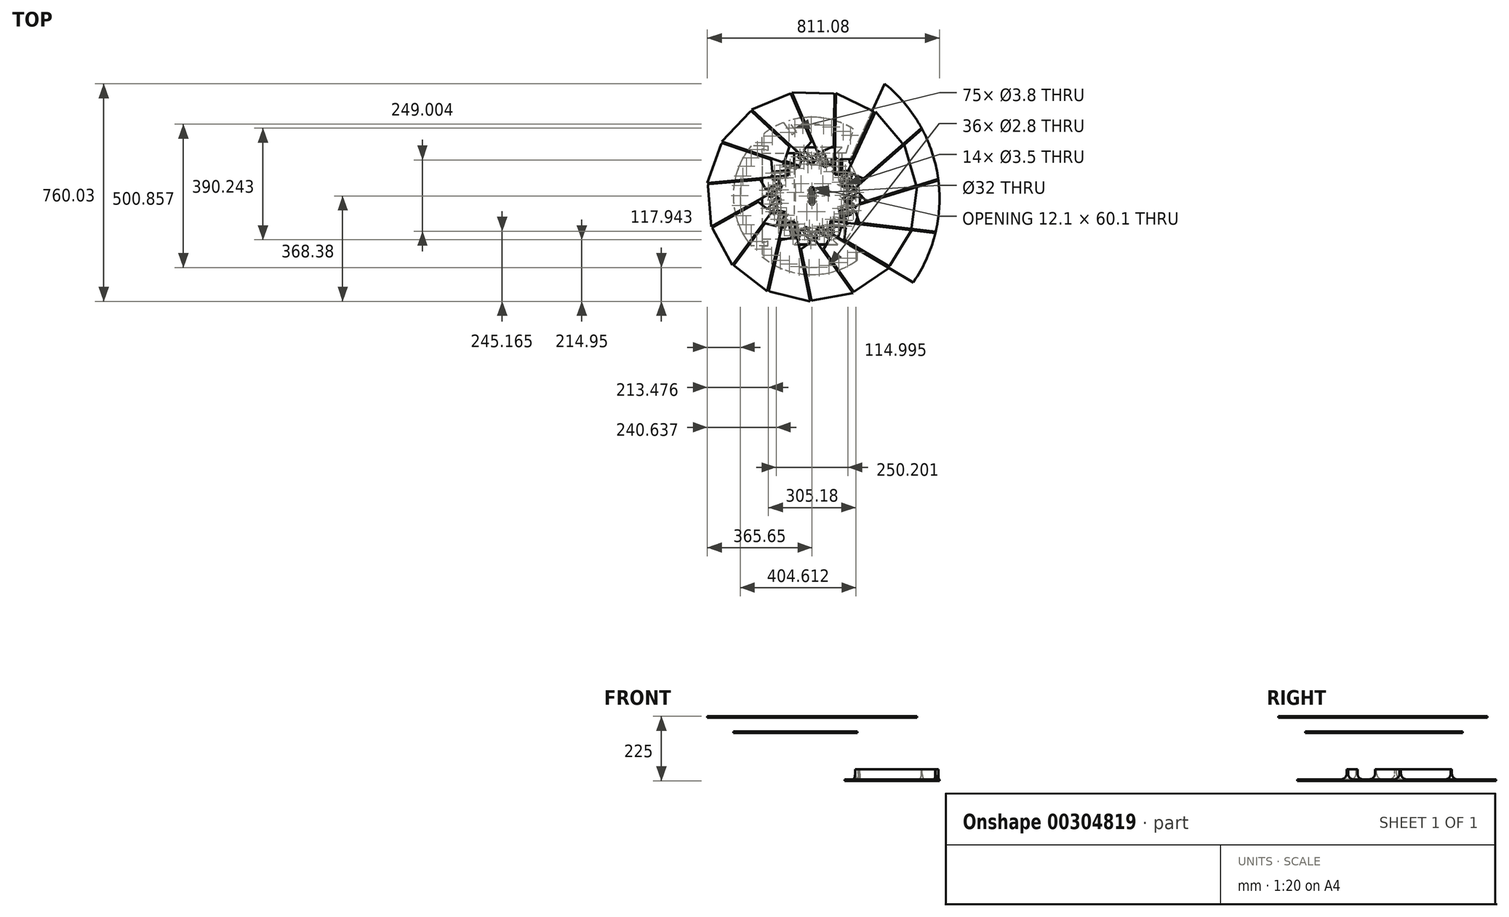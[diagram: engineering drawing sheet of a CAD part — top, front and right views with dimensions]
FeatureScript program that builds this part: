
annotation { "Feature Type Name" : "Feature", "Feature Type Description" : "" }
export const myFeature = defineFeature(function(context is Context, id is Id, definition is map)
    precondition{}
    {
        {
            var Q0;
            Q0=qCreatedBy(makeId("Top.planeOp"),FACE);
            var sketch = newSketch(context, id + "F0", { "sketchPlane" : qUnion([Q0])});
            skLineSegment(sketch, "E0", {"start": v(-97.83, 116.22) * mm, "end": v(-45.75, 98.54) * mm});
            skLineSegment(sketch, "E1", {"start": v(-78.6, 172.89) * mm, "end": v(-209.62, 294) * mm});
            skPoint(sketch, "E2.visualSharp", {"position": v(-213.23, 297.34) * mm});
            skArc(sketch, "E2.filletArc", {"start": v(-209.62, 294) * mm, "mid": v(-213.17, 295.33) * mm, "end": v(-216.63, 293.79) * mm});
            skLineSegment(sketch, "E3", {"start": v(-101.62, 117.5) * mm, "end": v(-315.6, 190.14) * mm});
            skLineSegment(sketch, "E4", {"start": v(-315.6, 190.14) * mm, "end": v(-216.63, 293.79) * mm});
            skLineSegment(sketch, "E5", {"start": v(-43.7, 117.06) * mm, "end": v(-91.98, 133.45) * mm});
            skLineSegment(sketch, "E6", {"start": v(-91.98, 133.45) * mm, "end": v(-78.6, 172.89) * mm});
            skLineSegment(sketch, "E7.bottom", {"start": v(4.05, -30.05) * mm, "end": v(-4.05, -30.05) * mm});
            skLineSegment(sketch, "E7.top", {"start": v(4.05, 30.05) * mm, "end": v(-4.05, 30.05) * mm});
            skLineSegment(sketch, "E7.left", {"start": v(6.05, -28.05) * mm, "end": v(6.05, 28.05) * mm});
            skLineSegment(sketch, "E7.right", {"start": v(-6.05, -28.05) * mm, "end": v(-6.05, 28.05) * mm});
            skPoint(sketch, "E7.middle", {"position": v(0, 0) * mm});
            skPoint(sketch, "E8.visualSharp", {"position": v(-6.05, 30.05) * mm});
            skArc(sketch, "E8.filletArc", {"start": v(-4.05, 30.05) * mm, "mid": v(-5.46, 29.46) * mm, "end": v(-6.05, 28.05) * mm});
            skPoint(sketch, "E9.visualSharp", {"position": v(6.05, 30.05) * mm});
            skArc(sketch, "E9.filletArc", {"start": v(6.05, 28.05) * mm, "mid": v(5.46, 29.46) * mm, "end": v(4.05, 30.05) * mm});
            skPoint(sketch, "E10.visualSharp", {"position": v(-6.05, -30.05) * mm});
            skArc(sketch, "E10.filletArc", {"start": v(-6.05, -28.05) * mm, "mid": v(-5.46, -29.46) * mm, "end": v(-4.05, -30.05) * mm});
            skPoint(sketch, "E11.visualSharp", {"position": v(6.05, -30.05) * mm});
            skArc(sketch, "E11.filletArc", {"start": v(4.05, -30.05) * mm, "mid": v(5.46, -29.46) * mm, "end": v(6.05, -28.05) * mm});
            skLineSegment(sketch, "E12.bottom", {"start": v(-101.63, 105.04) * mm, "end": v(-91.98, 133.45) * mm});
            skLineSegment(sketch, "E12.top", {"start": v(-53.33, 88.65) * mm, "end": v(-43.7, 117.06) * mm});
            skLineSegment(sketch, "E12.left", {"start": v(-101.63, 105.04) * mm, "end": v(-53.33, 88.65) * mm});
            skLineSegment(sketch, "E12.right", {"start": v(-91.98, 133.45) * mm, "end": v(-43.7, 117.06) * mm});
            skCircle(sketch, "E13", {"center": v(-51.93, 114.57) * mm, "radius": 1.75 * mm});
            skCircle(sketch, "E14", {"center": v(-86.96, 126.47) * mm, "radius": 1.9 * mm});
            skCircle(sketch, "E15", {"center": v(-93.4, 107.53) * mm, "radius": 1.9 * mm});
            skCircle(sketch, "E16", {"center": v(-58.36, 95.64) * mm, "radius": 1.9 * mm});
            skPoint(sketch, "E17", {"position": v(-77.48, 96.85) * mm});
            skLineSegment(sketch, "E18.left", {"start": v(-97.51, 117.17) * mm, "end": v(-49.22, 100.77) * mm});
            skLineSegment(sketch, "E18.right", {"start": v(-96.1, 121.33) * mm, "end": v(-47.8, 104.94) * mm});
            skLineSegment(sketch, "E19.0", {"start": v(-58.36, 95.64) * mm, "end": v(-51.93, 114.57) * mm, "construction": true});
            skLineSegment(sketch, "E20.0", {"start": v(-93.4, 107.53) * mm, "end": v(-86.96, 126.47) * mm, "construction": true});
            skLineSegment(sketch, "E21.0", {"start": v(-58.36, 95.64) * mm, "end": v(-93.4, 107.53) * mm, "construction": true});
            skLineSegment(sketch, "E22.0", {"start": v(-51.93, 114.57) * mm, "end": v(-86.96, 126.47) * mm, "construction": true});
            skPoint(sketch, "E23", {"position": v(-96.8, 119.25) * mm});
            skCircle(sketch, "E24", {"center": v(-75.87, 101.58) * mm, "radius": 1.9 * mm});
            skCircle(sketch, "E25", {"center": v(-69.45, 120.52) * mm, "radius": 1.9 * mm});
            skCircle(sketch, "E26.1.0", {"center": v(-130.88, 80.16) * mm, "radius": 1.9 * mm});
            skLineSegment(sketch, "E26.1.1", {"start": v(-92.2, 63.63) * mm, "end": v(-94.04, 83.55) * mm, "construction": true});
            skCircle(sketch, "E26.1.2", {"center": v(-112.46, 81.86) * mm, "radius": 1.9 * mm});
            skLineSegment(sketch, "E26.1.3", {"start": v(-92.2, 63.63) * mm, "end": v(-129.05, 60.25) * mm, "construction": true});
            skCircle(sketch, "E26.1.4", {"center": v(-110.63, 61.94) * mm, "radius": 1.9 * mm});
            skCircle(sketch, "E26.1.5", {"center": v(-92.2, 63.63) * mm, "radius": 1.9 * mm});
            skLineSegment(sketch, "E26.1.6", {"start": v(-135.57, 54.63) * mm, "end": v(-84.78, 59.3) * mm});
            skLineSegment(sketch, "E26.1.7", {"start": v(-135.57, 54.63) * mm, "end": v(-138.31, 84.5) * mm});
            skPoint(sketch, "E26.1.8", {"position": v(-136.94, 69.56) * mm});
            skLineSegment(sketch, "E26.1.9", {"start": v(-94.04, 83.55) * mm, "end": v(-130.88, 80.16) * mm, "construction": true});
            skLineSegment(sketch, "E26.1.10", {"start": v(-84.78, 59.3) * mm, "end": v(-87.53, 89.17) * mm});
            skCircle(sketch, "E26.1.11", {"center": v(-129.05, 60.25) * mm, "radius": 1.9 * mm});
            skLineSegment(sketch, "E26.1.12", {"start": v(-129.05, 60.25) * mm, "end": v(-130.88, 80.16) * mm, "construction": true});
            skPoint(sketch, "E26.1.13", {"position": v(-110.17, 56.96) * mm});
            skCircle(sketch, "E26.1.14", {"center": v(-94.04, 83.55) * mm, "radius": 1.75 * mm});
            skLineSegment(sketch, "E26.1.15", {"start": v(-138.31, 84.5) * mm, "end": v(-87.53, 89.17) * mm});
            skLineSegment(sketch, "E26.1.16", {"start": v(-136.74, 67.37) * mm, "end": v(-85.95, 72.04) * mm});
            skLineSegment(sketch, "E26.1.17", {"start": v(-137.14, 71.75) * mm, "end": v(-86.35, 76.42) * mm});
            skCircle(sketch, "E26.2.0", {"center": v(-152.17, 20) * mm, "radius": 1.9 * mm});
            skLineSegment(sketch, "E26.2.1", {"start": v(-110.12, 20.63) * mm, "end": v(-119.9, 38.08) * mm, "construction": true});
            skCircle(sketch, "E26.2.2", {"center": v(-136.03, 29.04) * mm, "radius": 1.9 * mm});
            skLineSegment(sketch, "E26.2.3", {"start": v(-110.12, 20.63) * mm, "end": v(-142.4, 2.55) * mm, "construction": true});
            skCircle(sketch, "E26.2.4", {"center": v(-126.26, 11.59) * mm, "radius": 1.9 * mm});
            skCircle(sketch, "E26.2.5", {"center": v(-110.12, 20.63) * mm, "radius": 1.9 * mm});
            skLineSegment(sketch, "E26.2.6", {"start": v(-146.07, -5.24) * mm, "end": v(-101.57, 19.68) * mm});
            skLineSegment(sketch, "E26.2.7", {"start": v(-146.07, -5.24) * mm, "end": v(-160.72, 20.94) * mm});
            skPoint(sketch, "E26.2.8", {"position": v(-153.4, 7.85) * mm});
            skLineSegment(sketch, "E26.2.9", {"start": v(-119.9, 38.08) * mm, "end": v(-152.17, 20) * mm, "construction": true});
            skLineSegment(sketch, "E26.2.10", {"start": v(-101.57, 19.68) * mm, "end": v(-116.23, 45.86) * mm});
            skCircle(sketch, "E26.2.11", {"center": v(-142.4, 2.55) * mm, "radius": 1.9 * mm});
            skLineSegment(sketch, "E26.2.12", {"start": v(-142.4, 2.55) * mm, "end": v(-152.17, 20) * mm, "construction": true});
            skPoint(sketch, "E26.2.13", {"position": v(-123.82, 7.22) * mm});
            skCircle(sketch, "E26.2.14", {"center": v(-119.9, 38.08) * mm, "radius": 1.75 * mm});
            skLineSegment(sketch, "E26.2.15", {"start": v(-160.72, 20.94) * mm, "end": v(-116.23, 45.86) * mm});
            skLineSegment(sketch, "E26.2.16", {"start": v(-152.32, 5.93) * mm, "end": v(-107.82, 30.85) * mm});
            skLineSegment(sketch, "E26.2.17", {"start": v(-154.47, 9.77) * mm, "end": v(-109.97, 34.7) * mm});
            skCircle(sketch, "E26.3.0", {"center": v(-147.15, -43.63) * mm, "radius": 1.9 * mm});
            skLineSegment(sketch, "E26.3.1", {"start": v(-108.99, -25.95) * mm, "end": v(-125.01, -13.98) * mm, "construction": true});
            skCircle(sketch, "E26.3.2", {"center": v(-136.08, -28.8) * mm, "radius": 1.9 * mm});
            skLineSegment(sketch, "E26.3.3", {"start": v(-108.99, -25.95) * mm, "end": v(-131.13, -55.6) * mm, "construction": true});
            skCircle(sketch, "E26.3.4", {"center": v(-120.06, -40.77) * mm, "radius": 1.9 * mm});
            skCircle(sketch, "E26.3.5", {"center": v(-108.99, -25.95) * mm, "radius": 1.9 * mm});
            skLineSegment(sketch, "E26.3.6", {"start": v(-131.3, -64.2) * mm, "end": v(-100.8, -23.33) * mm});
            skLineSegment(sketch, "E26.3.7", {"start": v(-131.3, -64.2) * mm, "end": v(-155.35, -46.24) * mm});
            skPoint(sketch, "E26.3.8", {"position": v(-143.33, -55.22) * mm});
            skLineSegment(sketch, "E26.3.9", {"start": v(-125.01, -13.98) * mm, "end": v(-147.15, -43.63) * mm, "construction": true});
            skLineSegment(sketch, "E26.3.10", {"start": v(-100.8, -23.33) * mm, "end": v(-124.83, -5.38) * mm});
            skCircle(sketch, "E26.3.11", {"center": v(-131.13, -55.6) * mm, "radius": 1.9 * mm});
            skLineSegment(sketch, "E26.3.12", {"start": v(-131.13, -55.6) * mm, "end": v(-147.15, -43.63) * mm, "construction": true});
            skPoint(sketch, "E26.3.13", {"position": v(-116.05, -43.76) * mm});
            skCircle(sketch, "E26.3.14", {"center": v(-125.01, -13.98) * mm, "radius": 1.75 * mm});
            skLineSegment(sketch, "E26.3.15", {"start": v(-155.35, -46.24) * mm, "end": v(-124.83, -5.38) * mm});
            skLineSegment(sketch, "E26.3.16", {"start": v(-141.56, -56.53) * mm, "end": v(-111.05, -15.67) * mm});
            skLineSegment(sketch, "E26.3.17", {"start": v(-145.09, -53.9) * mm, "end": v(-114.57, -13.04) * mm});
            skCircle(sketch, "E26.4.0", {"center": v(-116.68, -99.7) * mm, "radius": 1.9 * mm});
            skLineSegment(sketch, "E26.4.1", {"start": v(-89.01, -68.03) * mm, "end": v(-108.52, -63.62) * mm, "construction": true});
            skCircle(sketch, "E26.4.2", {"center": v(-112.6, -81.66) * mm, "radius": 1.9 * mm});
            skLineSegment(sketch, "E26.4.3", {"start": v(-89.01, -68.03) * mm, "end": v(-97.18, -104.12) * mm, "construction": true});
            skCircle(sketch, "E26.4.4", {"center": v(-93.1, -86.08) * mm, "radius": 1.9 * mm});
            skCircle(sketch, "E26.4.5", {"center": v(-89.01, -68.03) * mm, "radius": 1.9 * mm});
            skLineSegment(sketch, "E26.4.6", {"start": v(-93.85, -112.05) * mm, "end": v(-82.6, -62.3) * mm});
            skLineSegment(sketch, "E26.4.7", {"start": v(-93.85, -112.05) * mm, "end": v(-123.1, -105.43) * mm});
            skPoint(sketch, "E26.4.8", {"position": v(-108.48, -108.74) * mm});
            skLineSegment(sketch, "E26.4.9", {"start": v(-108.52, -63.62) * mm, "end": v(-116.68, -99.7) * mm, "construction": true});
            skLineSegment(sketch, "E26.4.10", {"start": v(-82.6, -62.3) * mm, "end": v(-111.85, -55.69) * mm});
            skCircle(sketch, "E26.4.11", {"center": v(-97.18, -104.12) * mm, "radius": 1.9 * mm});
            skLineSegment(sketch, "E26.4.12", {"start": v(-97.18, -104.12) * mm, "end": v(-116.68, -99.7) * mm, "construction": true});
            skPoint(sketch, "E26.4.13", {"position": v(-88.22, -87.18) * mm});
            skCircle(sketch, "E26.4.14", {"center": v(-108.52, -63.62) * mm, "radius": 1.75 * mm});
            skLineSegment(sketch, "E26.4.15", {"start": v(-123.1, -105.43) * mm, "end": v(-111.85, -55.69) * mm});
            skLineSegment(sketch, "E26.4.16", {"start": v(-106.33, -109.23) * mm, "end": v(-95.07, -59.48) * mm});
            skLineSegment(sketch, "E26.4.17", {"start": v(-110.62, -108.26) * mm, "end": v(-99.37, -58.51) * mm});
            skCircle(sketch, "E26.5.0", {"center": v(-66.04, -138.55) * mm, "radius": 1.9 * mm});
            skLineSegment(sketch, "E26.5.1", {"start": v(-53.65, -98.36) * mm, "end": v(-73.26, -102.26) * mm, "construction": true});
            skCircle(sketch, "E26.5.2", {"center": v(-69.65, -120.4) * mm, "radius": 1.9 * mm});
            skLineSegment(sketch, "E26.5.3", {"start": v(-53.65, -98.36) * mm, "end": v(-46.43, -134.64) * mm, "construction": true});
            skCircle(sketch, "E26.5.4", {"center": v(-50.04, -116.5) * mm, "radius": 1.9 * mm});
            skCircle(sketch, "E26.5.5", {"center": v(-53.65, -98.36) * mm, "radius": 1.9 * mm});
            skLineSegment(sketch, "E26.5.6", {"start": v(-40.16, -140.53) * mm, "end": v(-50.1, -90.51) * mm});
            skLineSegment(sketch, "E26.5.7", {"start": v(-40.16, -140.53) * mm, "end": v(-69.58, -146.39) * mm});
            skPoint(sketch, "E26.5.8", {"position": v(-54.87, -143.46) * mm});
            skLineSegment(sketch, "E26.5.9", {"start": v(-73.26, -102.26) * mm, "end": v(-66.04, -138.55) * mm, "construction": true});
            skLineSegment(sketch, "E26.5.10", {"start": v(-50.1, -90.51) * mm, "end": v(-79.53, -96.37) * mm});
            skCircle(sketch, "E26.5.11", {"center": v(-46.43, -134.64) * mm, "radius": 1.9 * mm});
            skLineSegment(sketch, "E26.5.12", {"start": v(-46.43, -134.64) * mm, "end": v(-66.04, -138.55) * mm, "construction": true});
            skPoint(sketch, "E26.5.13", {"position": v(-45.13, -115.52) * mm});
            skCircle(sketch, "E26.5.14", {"center": v(-73.26, -102.26) * mm, "radius": 1.75 * mm});
            skLineSegment(sketch, "E26.5.15", {"start": v(-69.58, -146.39) * mm, "end": v(-79.53, -96.37) * mm});
            skLineSegment(sketch, "E26.5.16", {"start": v(-52.71, -143.03) * mm, "end": v(-62.66, -93.01) * mm});
            skLineSegment(sketch, "E26.5.17", {"start": v(-57.03, -143.9) * mm, "end": v(-66.98, -93.87) * mm});
            skCircle(sketch, "E26.6.0", {"center": v(-3.98, -153.43) * mm, "radius": 1.9 * mm});
            skLineSegment(sketch, "E26.6.1", {"start": v(-9, -111.67) * mm, "end": v(-25.34, -123.21) * mm, "construction": true});
            skCircle(sketch, "E26.6.2", {"center": v(-14.66, -138.32) * mm, "radius": 1.9 * mm});
            skLineSegment(sketch, "E26.6.3", {"start": v(-9, -111.67) * mm, "end": v(12.35, -141.89) * mm, "construction": true});
            skCircle(sketch, "E26.6.4", {"center": v(1.67, -126.78) * mm, "radius": 1.9 * mm});
            skCircle(sketch, "E26.6.5", {"center": v(-9, -111.67) * mm, "radius": 1.9 * mm});
            skLineSegment(sketch, "E26.6.6", {"start": v(20.48, -144.72) * mm, "end": v(-8.96, -103.07) * mm});
            skLineSegment(sketch, "E26.6.7", {"start": v(20.48, -144.72) * mm, "end": v(-4.02, -162.03) * mm});
            skPoint(sketch, "E26.6.8", {"position": v(8.23, -153.38) * mm});
            skLineSegment(sketch, "E26.6.9", {"start": v(-25.34, -123.21) * mm, "end": v(-3.98, -153.43) * mm, "construction": true});
            skLineSegment(sketch, "E26.6.10", {"start": v(-8.96, -103.07) * mm, "end": v(-33.46, -120.38) * mm});
            skCircle(sketch, "E26.6.11", {"center": v(12.35, -141.89) * mm, "radius": 1.9 * mm});
            skLineSegment(sketch, "E26.6.12", {"start": v(12.35, -141.89) * mm, "end": v(-3.98, -153.43) * mm, "construction": true});
            skPoint(sketch, "E26.6.13", {"position": v(5.76, -123.9) * mm});
            skCircle(sketch, "E26.6.14", {"center": v(-25.34, -123.21) * mm, "radius": 1.75 * mm});
            skLineSegment(sketch, "E26.6.15", {"start": v(-4.02, -162.03) * mm, "end": v(-33.46, -120.38) * mm});
            skLineSegment(sketch, "E26.6.16", {"start": v(10.02, -152.1) * mm, "end": v(-19.41, -110.46) * mm});
            skLineSegment(sketch, "E26.6.17", {"start": v(6.43, -154.65) * mm, "end": v(-23, -113) * mm});
            skCircle(sketch, "E26.7.0", {"center": v(58.77, -141.78) * mm, "radius": 1.9 * mm});
            skLineSegment(sketch, "E26.7.1", {"start": v(37.2, -105.68) * mm, "end": v(26.97, -122.87) * mm, "construction": true});
            skCircle(sketch, "E26.7.2", {"center": v(42.87, -132.33) * mm, "radius": 1.9 * mm});
            skLineSegment(sketch, "E26.7.3", {"start": v(37.2, -105.68) * mm, "end": v(69, -124.6) * mm, "construction": true});
            skCircle(sketch, "E26.7.4", {"center": v(53.1, -115.14) * mm, "radius": 1.9 * mm});
            skCircle(sketch, "E26.7.5", {"center": v(37.2, -105.68) * mm, "radius": 1.9 * mm});
            skLineSegment(sketch, "E26.7.6", {"start": v(77.57, -123.88) * mm, "end": v(33.74, -97.8) * mm});
            skLineSegment(sketch, "E26.7.7", {"start": v(77.57, -123.88) * mm, "end": v(62.23, -149.66) * mm});
            skPoint(sketch, "E26.7.8", {"position": v(69.9, -136.77) * mm});
            skLineSegment(sketch, "E26.7.9", {"start": v(26.97, -122.87) * mm, "end": v(58.77, -141.78) * mm, "construction": true});
            skLineSegment(sketch, "E26.7.10", {"start": v(33.74, -97.8) * mm, "end": v(18.4, -123.58) * mm});
            skCircle(sketch, "E26.7.11", {"center": v(69, -124.6) * mm, "radius": 1.9 * mm});
            skLineSegment(sketch, "E26.7.12", {"start": v(69, -124.6) * mm, "end": v(58.77, -141.78) * mm, "construction": true});
            skPoint(sketch, "E26.7.13", {"position": v(55.65, -110.84) * mm});
            skCircle(sketch, "E26.7.14", {"center": v(26.97, -122.87) * mm, "radius": 1.75 * mm});
            skLineSegment(sketch, "E26.7.15", {"start": v(62.23, -149.66) * mm, "end": v(18.4, -123.58) * mm});
            skLineSegment(sketch, "E26.7.16", {"start": v(71.02, -134.88) * mm, "end": v(27.2, -108.8) * mm});
            skLineSegment(sketch, "E26.7.17", {"start": v(68.77, -138.66) * mm, "end": v(24.94, -112.58) * mm});
            skCircle(sketch, "E26.8.0", {"center": v(111.36, -105.62) * mm, "radius": 1.9 * mm});
            skLineSegment(sketch, "E26.8.1", {"start": v(76.96, -81.41) * mm, "end": v(74.61, -101.27) * mm, "construction": true});
            skCircle(sketch, "E26.8.2", {"center": v(92.99, -103.45) * mm, "radius": 1.9 * mm});
            skLineSegment(sketch, "E26.8.3", {"start": v(76.96, -81.41) * mm, "end": v(113.7, -85.76) * mm, "construction": true});
            skCircle(sketch, "E26.8.4", {"center": v(95.34, -83.59) * mm, "radius": 1.9 * mm});
            skCircle(sketch, "E26.8.5", {"center": v(76.96, -81.41) * mm, "radius": 1.9 * mm});
            skLineSegment(sketch, "E26.8.6", {"start": v(121.25, -81.62) * mm, "end": v(70.6, -75.62) * mm});
            skLineSegment(sketch, "E26.8.7", {"start": v(121.25, -81.62) * mm, "end": v(117.72, -111.41) * mm});
            skPoint(sketch, "E26.8.8", {"position": v(119.48, -96.52) * mm});
            skLineSegment(sketch, "E26.8.9", {"start": v(74.61, -101.27) * mm, "end": v(111.36, -105.62) * mm, "construction": true});
            skLineSegment(sketch, "E26.8.10", {"start": v(70.6, -75.62) * mm, "end": v(67.07, -105.42) * mm});
            skCircle(sketch, "E26.8.11", {"center": v(113.7, -85.76) * mm, "radius": 1.9 * mm});
            skLineSegment(sketch, "E26.8.12", {"start": v(113.7, -85.76) * mm, "end": v(111.36, -105.62) * mm, "construction": true});
            skPoint(sketch, "E26.8.13", {"position": v(95.92, -78.62) * mm});
            skCircle(sketch, "E26.8.14", {"center": v(74.61, -101.27) * mm, "radius": 1.75 * mm});
            skLineSegment(sketch, "E26.8.15", {"start": v(117.72, -111.41) * mm, "end": v(67.07, -105.42) * mm});
            skLineSegment(sketch, "E26.8.16", {"start": v(119.74, -94.33) * mm, "end": v(69.1, -88.34) * mm});
            skLineSegment(sketch, "E26.8.17", {"start": v(119.23, -98.7) * mm, "end": v(68.58, -92.7) * mm});
            skCircle(sketch, "E26.9.0", {"center": v(144.7, -51.2) * mm, "radius": 1.9 * mm});
            skLineSegment(sketch, "E26.9.1", {"start": v(103.42, -43.07) * mm, "end": v(109.35, -62.17) * mm, "construction": true});
            skCircle(sketch, "E26.9.2", {"center": v(127.02, -56.68) * mm, "radius": 1.9 * mm});
            skLineSegment(sketch, "E26.9.3", {"start": v(103.42, -43.07) * mm, "end": v(138.76, -32.1) * mm, "construction": true});
            skCircle(sketch, "E26.9.4", {"center": v(121.1, -37.58) * mm, "radius": 1.9 * mm});
            skCircle(sketch, "E26.9.5", {"center": v(103.42, -43.07) * mm, "radius": 1.9 * mm});
            skLineSegment(sketch, "E26.9.6", {"start": v(143.96, -25.25) * mm, "end": v(95.26, -40.37) * mm});
            skLineSegment(sketch, "E26.9.7", {"start": v(143.96, -25.25) * mm, "end": v(152.86, -53.9) * mm});
            skPoint(sketch, "E26.9.8", {"position": v(148.41, -39.57) * mm});
            skLineSegment(sketch, "E26.9.9", {"start": v(109.35, -62.17) * mm, "end": v(144.7, -51.2) * mm, "construction": true});
            skLineSegment(sketch, "E26.9.10", {"start": v(95.26, -40.37) * mm, "end": v(104.15, -69.02) * mm});
            skCircle(sketch, "E26.9.11", {"center": v(138.76, -32.1) * mm, "radius": 1.9 * mm});
            skLineSegment(sketch, "E26.9.12", {"start": v(138.76, -32.1) * mm, "end": v(144.7, -51.2) * mm, "construction": true});
            skPoint(sketch, "E26.9.13", {"position": v(119.6, -32.8) * mm});
            skCircle(sketch, "E26.9.14", {"center": v(109.35, -62.17) * mm, "radius": 1.75 * mm});
            skLineSegment(sketch, "E26.9.15", {"start": v(152.86, -53.9) * mm, "end": v(104.15, -69.02) * mm});
            skLineSegment(sketch, "E26.9.16", {"start": v(147.76, -37.47) * mm, "end": v(99.05, -52.6) * mm});
            skLineSegment(sketch, "E26.9.17", {"start": v(149.06, -41.67) * mm, "end": v(100.36, -56.8) * mm});
            skCircle(sketch, "E26.10.0", {"center": v(153, 12.08) * mm, "radius": 1.9 * mm});
            skLineSegment(sketch, "E26.10.1", {"start": v(112, 2.72) * mm, "end": v(125.19, -12.32) * mm, "construction": true});
            skCircle(sketch, "E26.10.2", {"center": v(139.1, -0.12) * mm, "radius": 1.9 * mm});
            skLineSegment(sketch, "E26.10.3", {"start": v(112, 2.72) * mm, "end": v(139.82, 27.12) * mm, "construction": true});
            skCircle(sketch, "E26.10.4", {"center": v(125.9, 14.92) * mm, "radius": 1.9 * mm});
            skCircle(sketch, "E26.10.5", {"center": v(112, 2.72) * mm, "radius": 1.9 * mm});
            skLineSegment(sketch, "E26.10.6", {"start": v(141.79, 35.5) * mm, "end": v(103.44, 1.86) * mm});
            skLineSegment(sketch, "E26.10.7", {"start": v(141.79, 35.5) * mm, "end": v(161.57, 12.93) * mm});
            skPoint(sketch, "E26.10.8", {"position": v(151.68, 24.21) * mm});
            skLineSegment(sketch, "E26.10.9", {"start": v(125.19, -12.32) * mm, "end": v(153, 12.08) * mm, "construction": true});
            skLineSegment(sketch, "E26.10.10", {"start": v(103.44, 1.86) * mm, "end": v(123.22, -20.7) * mm});
            skCircle(sketch, "E26.10.11", {"center": v(139.82, 27.12) * mm, "radius": 1.9 * mm});
            skLineSegment(sketch, "E26.10.12", {"start": v(139.82, 27.12) * mm, "end": v(153, 12.08) * mm, "construction": true});
            skPoint(sketch, "E26.10.13", {"position": v(122.61, 18.68) * mm});
            skCircle(sketch, "E26.10.14", {"center": v(125.19, -12.32) * mm, "radius": 1.75 * mm});
            skLineSegment(sketch, "E26.10.15", {"start": v(161.57, 12.93) * mm, "end": v(123.22, -20.7) * mm});
            skLineSegment(sketch, "E26.10.16", {"start": v(150.22, 25.87) * mm, "end": v(111.88, -7.76) * mm});
            skLineSegment(sketch, "E26.10.17", {"start": v(153.13, 22.56) * mm, "end": v(114.78, -11.07) * mm});
            skCircle(sketch, "E26.11.0", {"center": v(134.86, 73.27) * mm, "radius": 1.9 * mm});
            skLineSegment(sketch, "E26.11.1", {"start": v(101.21, 48.04) * mm, "end": v(119.37, 39.67) * mm, "construction": true});
            skCircle(sketch, "E26.11.2", {"center": v(127.12, 56.47) * mm, "radius": 1.9 * mm});
            skLineSegment(sketch, "E26.11.3", {"start": v(101.21, 48.04) * mm, "end": v(116.7, 81.64) * mm, "construction": true});
            skCircle(sketch, "E26.11.4", {"center": v(108.96, 64.84) * mm, "radius": 1.9 * mm});
            skCircle(sketch, "E26.11.5", {"center": v(101.21, 48.04) * mm, "radius": 1.9 * mm});
            skLineSegment(sketch, "E26.11.6", {"start": v(115.1, 90.1) * mm, "end": v(93.74, 43.78) * mm});
            skLineSegment(sketch, "E26.11.7", {"start": v(115.1, 90.1) * mm, "end": v(142.34, 77.53) * mm});
            skPoint(sketch, "E26.11.8", {"position": v(128.71, 83.81) * mm});
            skLineSegment(sketch, "E26.11.9", {"start": v(119.37, 39.67) * mm, "end": v(134.86, 73.27) * mm, "construction": true});
            skLineSegment(sketch, "E26.11.10", {"start": v(93.74, 43.78) * mm, "end": v(120.98, 31.22) * mm});
            skCircle(sketch, "E26.11.11", {"center": v(116.7, 81.64) * mm, "radius": 1.9 * mm});
            skLineSegment(sketch, "E26.11.12", {"start": v(116.7, 81.64) * mm, "end": v(134.86, 73.27) * mm, "construction": true});
            skPoint(sketch, "E26.11.13", {"position": v(104.42, 66.93) * mm});
            skCircle(sketch, "E26.11.14", {"center": v(119.37, 39.67) * mm, "radius": 1.75 * mm});
            skLineSegment(sketch, "E26.11.15", {"start": v(142.34, 77.53) * mm, "end": v(120.98, 31.22) * mm});
            skLineSegment(sketch, "E26.11.16", {"start": v(126.72, 84.73) * mm, "end": v(105.36, 38.42) * mm});
            skLineSegment(sketch, "E26.11.17", {"start": v(130.71, 82.9) * mm, "end": v(109.36, 36.57) * mm});
            skCircle(sketch, "E26.12.0", {"center": v(93.4, 121.79) * mm, "radius": 1.9 * mm});
            skLineSegment(sketch, "E26.12.1", {"start": v(72.92, 85.05) * mm, "end": v(92.92, 84.8) * mm, "construction": true});
            skCircle(sketch, "E26.12.2", {"center": v(93.16, 103.29) * mm, "radius": 1.9 * mm});
            skLineSegment(sketch, "E26.12.3", {"start": v(72.92, 85.05) * mm, "end": v(73.4, 122.05) * mm, "construction": true});
            skCircle(sketch, "E26.12.4", {"center": v(73.16, 103.55) * mm, "radius": 1.9 * mm});
            skCircle(sketch, "E26.12.5", {"center": v(72.92, 85.05) * mm, "radius": 1.9 * mm});
            skLineSegment(sketch, "E26.12.6", {"start": v(68.5, 129.11) * mm, "end": v(67.83, 78.12) * mm});
            skLineSegment(sketch, "E26.12.7", {"start": v(68.5, 129.11) * mm, "end": v(98.5, 128.72) * mm});
            skPoint(sketch, "E26.12.8", {"position": v(83.5, 128.92) * mm});
            skLineSegment(sketch, "E26.12.9", {"start": v(92.92, 84.8) * mm, "end": v(93.4, 121.79) * mm, "construction": true});
            skLineSegment(sketch, "E26.12.10", {"start": v(67.83, 78.12) * mm, "end": v(97.83, 77.73) * mm});
            skCircle(sketch, "E26.12.11", {"center": v(73.4, 122.05) * mm, "radius": 1.9 * mm});
            skLineSegment(sketch, "E26.12.12", {"start": v(73.4, 122.05) * mm, "end": v(93.4, 121.79) * mm, "construction": true});
            skPoint(sketch, "E26.12.13", {"position": v(68.16, 103.62) * mm});
            skCircle(sketch, "E26.12.14", {"center": v(92.92, 84.8) * mm, "radius": 1.75 * mm});
            skLineSegment(sketch, "E26.12.15", {"start": v(98.5, 128.72) * mm, "end": v(97.83, 77.73) * mm});
            skLineSegment(sketch, "E26.12.16", {"start": v(81.3, 128.95) * mm, "end": v(80.63, 77.95) * mm});
            skLineSegment(sketch, "E26.12.17", {"start": v(85.7, 128.89) * mm, "end": v(85.03, 77.9) * mm});
            skCircle(sketch, "E26.13.0", {"center": v(35.8, 149.25) * mm, "radius": 1.9 * mm});
            skLineSegment(sketch, "E26.13.1", {"start": v(32.02, 107.36) * mm, "end": v(50.4, 115.25) * mm, "construction": true});
            skCircle(sketch, "E26.13.2", {"center": v(43.1, 132.25) * mm, "radius": 1.9 * mm});
            skLineSegment(sketch, "E26.13.3", {"start": v(32.02, 107.36) * mm, "end": v(17.42, 141.35) * mm, "construction": true});
            skCircle(sketch, "E26.13.4", {"center": v(24.72, 124.36) * mm, "radius": 1.9 * mm});
            skCircle(sketch, "E26.13.5", {"center": v(32.02, 107.36) * mm, "radius": 1.9 * mm});
            skLineSegment(sketch, "E26.13.6", {"start": v(10.06, 145.81) * mm, "end": v(30.2, 98.95) * mm});
            skLineSegment(sketch, "E26.13.7", {"start": v(10.06, 145.81) * mm, "end": v(37.62, 157.66) * mm});
            skPoint(sketch, "E26.13.8", {"position": v(23.84, 151.73) * mm});
            skLineSegment(sketch, "E26.13.9", {"start": v(50.4, 115.25) * mm, "end": v(35.8, 149.25) * mm, "construction": true});
            skLineSegment(sketch, "E26.13.10", {"start": v(30.2, 98.95) * mm, "end": v(57.76, 110.8) * mm});
            skCircle(sketch, "E26.13.11", {"center": v(17.42, 141.35) * mm, "radius": 1.9 * mm});
            skLineSegment(sketch, "E26.13.12", {"start": v(17.42, 141.35) * mm, "end": v(35.8, 149.25) * mm, "construction": true});
            skPoint(sketch, "E26.13.13", {"position": v(20.13, 122.38) * mm});
            skCircle(sketch, "E26.13.14", {"center": v(50.4, 115.25) * mm, "radius": 1.75 * mm});
            skLineSegment(sketch, "E26.13.15", {"start": v(37.62, 157.66) * mm, "end": v(57.76, 110.8) * mm});
            skLineSegment(sketch, "E26.13.16", {"start": v(21.82, 150.87) * mm, "end": v(41.95, 104) * mm});
            skLineSegment(sketch, "E26.13.17", {"start": v(25.86, 152.6) * mm, "end": v(46, 105.74) * mm});
            skCircle(sketch, "E26.14.0", {"center": v(-28, 150.9) * mm, "radius": 1.9 * mm});
            skLineSegment(sketch, "E26.14.1", {"start": v(-14.41, 111.1) * mm, "end": v(-0.84, 125.79) * mm, "construction": true});
            skCircle(sketch, "E26.14.2", {"center": v(-14.42, 138.35) * mm, "radius": 1.9 * mm});
            skLineSegment(sketch, "E26.14.3", {"start": v(-14.41, 111.1) * mm, "end": v(-41.58, 136.22) * mm, "construction": true});
            skCircle(sketch, "E26.14.4", {"center": v(-28, 123.66) * mm, "radius": 1.9 * mm});
            skCircle(sketch, "E26.14.5", {"center": v(-14.41, 111.1) * mm, "radius": 1.9 * mm});
            skLineSegment(sketch, "E26.14.6", {"start": v(-50.12, 137.3) * mm, "end": v(-12.67, 102.68) * mm});
            skLineSegment(sketch, "E26.14.7", {"start": v(-50.12, 137.3) * mm, "end": v(-29.75, 159.33) * mm});
            skPoint(sketch, "E26.14.8", {"position": v(-39.93, 148.31) * mm});
            skLineSegment(sketch, "E26.14.9", {"start": v(-0.84, 125.79) * mm, "end": v(-28, 150.9) * mm, "construction": true});
            skLineSegment(sketch, "E26.14.10", {"start": v(-12.67, 102.68) * mm, "end": v(7.7, 124.7) * mm});
            skCircle(sketch, "E26.14.11", {"center": v(-41.58, 136.22) * mm, "radius": 1.9 * mm});
            skLineSegment(sketch, "E26.14.12", {"start": v(-41.58, 136.22) * mm, "end": v(-28, 150.9) * mm, "construction": true});
            skPoint(sketch, "E26.14.13", {"position": v(-31.4, 119.99) * mm});
            skCircle(sketch, "E26.14.14", {"center": v(-0.84, 125.79) * mm, "radius": 1.75 * mm});
            skLineSegment(sketch, "E26.14.15", {"start": v(-29.75, 159.33) * mm, "end": v(7.7, 124.7) * mm});
            skLineSegment(sketch, "E26.14.16", {"start": v(-41.43, 146.7) * mm, "end": v(-3.98, 112.08) * mm});
            skLineSegment(sketch, "E26.14.17", {"start": v(-38.44, 149.93) * mm, "end": v(-1, 115.31) * mm});
            skLineSegment(sketch, "E27", {"start": v(-101.62, 117.5) * mm, "end": v(-99.57, 123.56) * mm});
            skLineSegment(sketch, "E28", {"start": v(-99.57, 123.56) * mm, "end": v(-47.48, 105.89) * mm});
            skLineSegment(sketch, "E29", {"start": v(-47.48, 105.89) * mm, "end": v(-43.7, 117.06) * mm});
            skLineSegment(sketch, "E30", {"start": v(-43.7, 117.06) * mm, "end": v(-47.48, 105.89) * mm});
            skLineSegment(sketch, "E31", {"start": v(-97.83, 116.22) * mm, "end": v(-101.63, 105.04) * mm});
            skLineSegment(sketch, "E32", {"start": v(-45.75, 98.54) * mm, "end": v(-36.78, 124.97) * mm});
            skLineSegment(sketch, "E33", {"start": v(-36.78, 124.97) * mm, "end": v(-50.12, 137.3) * mm});
            skLineSegment(sketch, "E34.1.0", {"start": v(-81.88, 71.41) * mm, "end": v(-84.43, 99.2) * mm});
            skLineSegment(sketch, "E34.1.1", {"start": v(-136.65, 66.38) * mm, "end": v(-81.88, 71.41) * mm});
            skLineSegment(sketch, "E34.1.2", {"start": v(-136.65, 66.38) * mm, "end": v(-135.57, 54.63) * mm});
            skLineSegment(sketch, "E34.1.3", {"start": v(-84.43, 99.2) * mm, "end": v(-101.63, 105.04) * mm});
            skLineSegment(sketch, "E34.1.4", {"start": v(-140.63, 66.01) * mm, "end": v(-365.65, 45.34) * mm});
            skPoint(sketch, "E34.1.5", {"position": v(-315.73, 184.9) * mm});
            skLineSegment(sketch, "E34.1.6", {"start": v(-142.12, 125.97) * mm, "end": v(-311.08, 183.32) * mm});
            skLineSegment(sketch, "E34.1.7", {"start": v(-365.65, 45.34) * mm, "end": v(-317.4, 180.28) * mm});
            skArc(sketch, "E34.1.8", {"start": v(-311.08, 183.32) * mm, "mid": v(-314.86, 183.1) * mm, "end": v(-317.4, 180.28) * mm});
            skLineSegment(sketch, "E34.1.9", {"start": v(-138.31, 84.5) * mm, "end": v(-142.12, 125.97) * mm});
            skLineSegment(sketch, "E34.1.10", {"start": v(-140.63, 66.01) * mm, "end": v(-141.22, 72.38) * mm});
            skLineSegment(sketch, "E34.1.11", {"start": v(-141.22, 72.38) * mm, "end": v(-86.45, 77.42) * mm});
            skLineSegment(sketch, "E34.1.12", {"start": v(-87.53, 89.17) * mm, "end": v(-138.31, 84.5) * mm});
            skLineSegment(sketch, "E34.1.13", {"start": v(-87.53, 89.17) * mm, "end": v(-86.45, 77.42) * mm});
            skLineSegment(sketch, "E34.2.0", {"start": v(-103.84, 31.93) * mm, "end": v(-117.48, 56.29) * mm});
            skLineSegment(sketch, "E34.2.1", {"start": v(-151.83, 5.06) * mm, "end": v(-103.84, 31.93) * mm});
            skLineSegment(sketch, "E34.2.2", {"start": v(-151.83, 5.06) * mm, "end": v(-146.07, -5.24) * mm});
            skLineSegment(sketch, "E34.2.3", {"start": v(-117.48, 56.29) * mm, "end": v(-135.57, 54.63) * mm});
            skLineSegment(sketch, "E34.2.4", {"start": v(-155.32, 3.1) * mm, "end": v(-352.47, -107.3) * mm});
            skPoint(sketch, "E34.2.5", {"position": v(-363.64, 40.5) * mm});
            skLineSegment(sketch, "E34.2.6", {"start": v(-181.07, 57.27) * mm, "end": v(-358.75, 40.95) * mm});
            skLineSegment(sketch, "E34.2.7", {"start": v(-352.47, -107.3) * mm, "end": v(-363.28, 35.6) * mm});
            skArc(sketch, "E34.2.8", {"start": v(-358.75, 40.95) * mm, "mid": v(-362.1, 39.2) * mm, "end": v(-363.28, 35.6) * mm});
            skLineSegment(sketch, "E34.2.9", {"start": v(-160.72, 20.94) * mm, "end": v(-181.07, 57.27) * mm});
            skLineSegment(sketch, "E34.2.10", {"start": v(-155.32, 3.1) * mm, "end": v(-158.45, 8.69) * mm});
            skLineSegment(sketch, "E34.2.11", {"start": v(-158.45, 8.69) * mm, "end": v(-110.46, 35.56) * mm});
            skLineSegment(sketch, "E34.2.12", {"start": v(-116.23, 45.86) * mm, "end": v(-160.72, 20.94) * mm});
            skLineSegment(sketch, "E34.2.13", {"start": v(-116.23, 45.86) * mm, "end": v(-110.46, 35.56) * mm});
            skLineSegment(sketch, "E34.3.0", {"start": v(-107.85, -13.06) * mm, "end": v(-130.22, 3.64) * mm});
            skLineSegment(sketch, "E34.3.1", {"start": v(-140.76, -57.13) * mm, "end": v(-107.85, -13.06) * mm});
            skLineSegment(sketch, "E34.3.2", {"start": v(-140.76, -57.13) * mm, "end": v(-131.3, -64.2) * mm});
            skLineSegment(sketch, "E34.3.3", {"start": v(-130.22, 3.64) * mm, "end": v(-146.07, -5.24) * mm});
            skLineSegment(sketch, "E34.3.4", {"start": v(-143.16, -60.34) * mm, "end": v(-278.36, -241.4) * mm});
            skPoint(sketch, "E34.3.5", {"position": v(-348.68, -110.9) * mm});
            skLineSegment(sketch, "E34.3.6", {"start": v(-188.71, -21.33) * mm, "end": v(-344.39, -108.5) * mm});
            skLineSegment(sketch, "E34.3.7", {"start": v(-278.36, -241.4) * mm, "end": v(-346.35, -115.24) * mm});
            skArc(sketch, "E34.3.8", {"start": v(-344.39, -108.5) * mm, "mid": v(-346.75, -111.47) * mm, "end": v(-346.35, -115.24) * mm});
            skLineSegment(sketch, "E34.3.9", {"start": v(-155.35, -46.24) * mm, "end": v(-188.71, -21.33) * mm});
            skLineSegment(sketch, "E34.3.10", {"start": v(-143.16, -60.34) * mm, "end": v(-148.28, -56.5) * mm});
            skLineSegment(sketch, "E34.3.11", {"start": v(-148.28, -56.5) * mm, "end": v(-115.38, -12.44) * mm});
            skLineSegment(sketch, "E34.3.12", {"start": v(-124.83, -5.38) * mm, "end": v(-155.35, -46.24) * mm});
            skLineSegment(sketch, "E34.3.13", {"start": v(-124.83, -5.38) * mm, "end": v(-115.38, -12.44) * mm});
            skLineSegment(sketch, "E34.4.0", {"start": v(-93.22, -55.8) * mm, "end": v(-120.44, -49.64) * mm});
            skLineSegment(sketch, "E34.4.1", {"start": v(-105.36, -109.45) * mm, "end": v(-93.22, -55.8) * mm});
            skLineSegment(sketch, "E34.4.2", {"start": v(-105.36, -109.45) * mm, "end": v(-93.85, -112.05) * mm});
            skLineSegment(sketch, "E34.4.3", {"start": v(-120.44, -49.64) * mm, "end": v(-131.3, -64.2) * mm});
            skLineSegment(sketch, "E34.4.4", {"start": v(-106.24, -113.35) * mm, "end": v(-156.1, -333.74) * mm});
            skPoint(sketch, "E34.4.5", {"position": v(-273.42, -243.14) * mm});
            skLineSegment(sketch, "E34.4.6", {"start": v(-163.72, -96.24) * mm, "end": v(-270.48, -239.2) * mm});
            skLineSegment(sketch, "E34.4.7", {"start": v(-156.1, -333.74) * mm, "end": v(-269.54, -246.15) * mm});
            skArc(sketch, "E34.4.8", {"start": v(-270.48, -239.2) * mm, "mid": v(-271.43, -242.87) * mm, "end": v(-269.54, -246.15) * mm});
            skLineSegment(sketch, "E34.4.9", {"start": v(-123.1, -105.43) * mm, "end": v(-163.72, -96.24) * mm});
            skLineSegment(sketch, "E34.4.10", {"start": v(-106.24, -113.35) * mm, "end": v(-112.48, -111.94) * mm});
            skLineSegment(sketch, "E34.4.11", {"start": v(-112.48, -111.94) * mm, "end": v(-100.34, -58.3) * mm});
            skLineSegment(sketch, "E34.4.12", {"start": v(-111.85, -55.69) * mm, "end": v(-123.1, -105.43) * mm});
            skLineSegment(sketch, "E34.4.13", {"start": v(-111.85, -55.69) * mm, "end": v(-100.34, -58.3) * mm});
            skLineSegment(sketch, "E34.5.0", {"start": v(-62.46, -88.9) * mm, "end": v(-89.84, -94.34) * mm});
            skLineSegment(sketch, "E34.5.1", {"start": v(-51.73, -142.84) * mm, "end": v(-62.46, -88.9) * mm});
            skLineSegment(sketch, "E34.5.2", {"start": v(-51.73, -142.84) * mm, "end": v(-40.16, -140.53) * mm});
            skLineSegment(sketch, "E34.5.3", {"start": v(-89.84, -94.34) * mm, "end": v(-93.85, -112.05) * mm});
            skLineSegment(sketch, "E34.5.4", {"start": v(-50.95, -146.76) * mm, "end": v(-6.87, -368.38) * mm});
            skPoint(sketch, "E34.5.5", {"position": v(-150.89, -333.33) * mm});
            skLineSegment(sketch, "E34.5.6", {"start": v(-110.43, -154.51) * mm, "end": v(-149.8, -328.54) * mm});
            skLineSegment(sketch, "E34.5.7", {"start": v(-6.87, -368.38) * mm, "end": v(-146.12, -334.5) * mm});
            skArc(sketch, "E34.5.8", {"start": v(-149.8, -328.54) * mm, "mid": v(-149.18, -332.27) * mm, "end": v(-146.12, -334.5) * mm});
            skLineSegment(sketch, "E34.5.9", {"start": v(-69.58, -146.39) * mm, "end": v(-110.43, -154.51) * mm});
            skLineSegment(sketch, "E34.5.10", {"start": v(-50.95, -146.76) * mm, "end": v(-57.23, -148) * mm});
            skLineSegment(sketch, "E34.5.11", {"start": v(-57.23, -148) * mm, "end": v(-67.96, -94.07) * mm});
            skLineSegment(sketch, "E34.5.12", {"start": v(-79.53, -96.37) * mm, "end": v(-69.58, -146.39) * mm});
            skLineSegment(sketch, "E34.5.13", {"start": v(-79.53, -96.37) * mm, "end": v(-67.96, -94.07) * mm});
            skLineSegment(sketch, "E34.6.0", {"start": v(-20.9, -106.61) * mm, "end": v(-43.7, -122.72) * mm});
            skLineSegment(sketch, "E34.6.1", {"start": v(10.84, -151.53) * mm, "end": v(-20.9, -106.61) * mm});
            skLineSegment(sketch, "E34.6.2", {"start": v(10.84, -151.53) * mm, "end": v(20.48, -144.72) * mm});
            skLineSegment(sketch, "E34.6.3", {"start": v(-43.7, -122.72) * mm, "end": v(-40.16, -140.53) * mm});
            skLineSegment(sketch, "E34.6.4", {"start": v(13.15, -154.8) * mm, "end": v(143.56, -339.33) * mm});
            skPoint(sketch, "E34.6.5", {"position": v(-2.27, -365.88) * mm});
            skLineSegment(sketch, "E34.6.6", {"start": v(-38.03, -186.07) * mm, "end": v(-3.22, -361.06) * mm});
            skLineSegment(sketch, "E34.6.7", {"start": v(143.56, -339.33) * mm, "end": v(2.57, -365) * mm});
            skArc(sketch, "E34.6.8", {"start": v(-3.22, -361.06) * mm, "mid": v(-1.13, -364.22) * mm, "end": v(2.57, -365) * mm});
            skLineSegment(sketch, "E34.6.9", {"start": v(-4.02, -162.03) * mm, "end": v(-38.03, -186.07) * mm});
            skLineSegment(sketch, "E34.6.10", {"start": v(13.15, -154.8) * mm, "end": v(7.92, -158.49) * mm});
            skLineSegment(sketch, "E34.6.11", {"start": v(7.92, -158.49) * mm, "end": v(-23.82, -113.57) * mm});
            skLineSegment(sketch, "E34.6.12", {"start": v(-33.46, -120.38) * mm, "end": v(-4.02, -162.03) * mm});
            skLineSegment(sketch, "E34.6.13", {"start": v(-33.46, -120.38) * mm, "end": v(-23.82, -113.57) * mm});
            skLineSegment(sketch, "E34.7.0", {"start": v(24.27, -105.9) * mm, "end": v(10, -129.89) * mm});
            skLineSegment(sketch, "E34.7.1", {"start": v(71.53, -134.02) * mm, "end": v(24.27, -105.9) * mm});
            skLineSegment(sketch, "E34.7.2", {"start": v(71.53, -134.02) * mm, "end": v(77.57, -123.88) * mm});
            skLineSegment(sketch, "E34.7.3", {"start": v(10, -129.89) * mm, "end": v(20.48, -144.72) * mm});
            skLineSegment(sketch, "E34.7.4", {"start": v(74.97, -136.06) * mm, "end": v(269.17, -251.6) * mm});
            skPoint(sketch, "E34.7.5", {"position": v(146.75, -335.17) * mm});
            skLineSegment(sketch, "E34.7.6", {"start": v(40.94, -185.45) * mm, "end": v(143.91, -331.16) * mm});
            skLineSegment(sketch, "E34.7.7", {"start": v(269.17, -251.6) * mm, "end": v(150.8, -332.4) * mm});
            skArc(sketch, "E34.7.8", {"start": v(143.91, -331.16) * mm, "mid": v(147.1, -333.2) * mm, "end": v(150.8, -332.4) * mm});
            skLineSegment(sketch, "E34.7.9", {"start": v(62.23, -149.66) * mm, "end": v(40.94, -185.45) * mm});
            skLineSegment(sketch, "E34.7.10", {"start": v(74.97, -136.06) * mm, "end": v(71.7, -141.57) * mm});
            skLineSegment(sketch, "E34.7.11", {"start": v(71.7, -141.57) * mm, "end": v(24.43, -113.44) * mm});
            skLineSegment(sketch, "E34.7.12", {"start": v(18.4, -123.58) * mm, "end": v(62.23, -149.66) * mm});
            skLineSegment(sketch, "E34.7.13", {"start": v(18.4, -123.58) * mm, "end": v(24.43, -113.44) * mm});
            skLineSegment(sketch, "E34.8.0", {"start": v(65.24, -86.87) * mm, "end": v(61.96, -114.6) * mm});
            skLineSegment(sketch, "E34.8.1", {"start": v(119.86, -93.34) * mm, "end": v(65.24, -86.87) * mm});
            skLineSegment(sketch, "E34.8.2", {"start": v(119.86, -93.34) * mm, "end": v(121.25, -81.62) * mm});
            skLineSegment(sketch, "E34.8.3", {"start": v(61.96, -114.6) * mm, "end": v(77.57, -123.88) * mm});
            skLineSegment(sketch, "E34.8.4", {"start": v(123.83, -93.8) * mm, "end": v(348.23, -120.37) * mm});
            skPoint(sketch, "E34.8.5", {"position": v(270.39, -246.5) * mm});
            skLineSegment(sketch, "E34.8.6", {"start": v(112.83, -152.77) * mm, "end": v(266.17, -244) * mm});
            skLineSegment(sketch, "E34.8.7", {"start": v(348.23, -120.37) * mm, "end": v(272.97, -242.33) * mm});
            skArc(sketch, "E34.8.8", {"start": v(266.17, -244) * mm, "mid": v(269.91, -244.56) * mm, "end": v(272.97, -242.33) * mm});
            skLineSegment(sketch, "E34.8.9", {"start": v(117.72, -111.41) * mm, "end": v(112.83, -152.77) * mm});
            skLineSegment(sketch, "E34.8.10", {"start": v(123.83, -93.8) * mm, "end": v(123.08, -100.16) * mm});
            skLineSegment(sketch, "E34.8.11", {"start": v(123.08, -100.16) * mm, "end": v(68.46, -93.7) * mm});
            skLineSegment(sketch, "E34.8.12", {"start": v(67.07, -105.42) * mm, "end": v(117.72, -111.41) * mm});
            skLineSegment(sketch, "E34.8.13", {"start": v(67.07, -105.42) * mm, "end": v(68.46, -93.7) * mm});
            skLineSegment(sketch, "E34.9.0", {"start": v(94.94, -52.83) * mm, "end": v(103.21, -79.48) * mm});
            skLineSegment(sketch, "E34.9.1", {"start": v(147.46, -36.52) * mm, "end": v(94.94, -52.83) * mm});
            skLineSegment(sketch, "E34.9.2", {"start": v(147.46, -36.52) * mm, "end": v(143.96, -25.25) * mm});
            skLineSegment(sketch, "E34.9.3", {"start": v(103.21, -79.48) * mm, "end": v(121.25, -81.62) * mm});
            skLineSegment(sketch, "E34.9.4", {"start": v(151.28, -35.33) * mm, "end": v(367.08, 31.68) * mm});
            skPoint(sketch, "E34.9.5", {"position": v(347.28, -115.22) * mm});
            skLineSegment(sketch, "E34.9.6", {"start": v(165.2, -93.67) * mm, "end": v(342.4, -114.64) * mm});
            skLineSegment(sketch, "E34.9.7", {"start": v(367.08, 31.68) * mm, "end": v(347.94, -110.35) * mm});
            skArc(sketch, "E34.9.8", {"start": v(342.4, -114.64) * mm, "mid": v(346.05, -113.63) * mm, "end": v(347.94, -110.35) * mm});
            skLineSegment(sketch, "E34.9.9", {"start": v(152.86, -53.9) * mm, "end": v(165.2, -93.67) * mm});
            skLineSegment(sketch, "E34.9.10", {"start": v(151.28, -35.33) * mm, "end": v(153.18, -41.44) * mm});
            skLineSegment(sketch, "E34.9.11", {"start": v(153.18, -41.44) * mm, "end": v(100.65, -57.75) * mm});
            skLineSegment(sketch, "E34.9.12", {"start": v(104.15, -69.02) * mm, "end": v(152.86, -53.9) * mm});
            skLineSegment(sketch, "E34.9.13", {"start": v(104.15, -69.02) * mm, "end": v(100.65, -57.75) * mm});
            skLineSegment(sketch, "E34.10.0", {"start": v(108.21, -9.65) * mm, "end": v(126.62, -30.63) * mm});
            skLineSegment(sketch, "E34.10.1", {"start": v(149.57, 26.62) * mm, "end": v(108.21, -9.65) * mm});
            skLineSegment(sketch, "E34.10.2", {"start": v(149.57, 26.62) * mm, "end": v(141.79, 35.5) * mm});
            skLineSegment(sketch, "E34.10.3", {"start": v(126.62, -30.63) * mm, "end": v(143.96, -25.25) * mm});
            skLineSegment(sketch, "E34.10.4", {"start": v(152.57, 29.26) * mm, "end": v(322.46, 178.24) * mm});
            skPoint(sketch, "E34.10.5", {"position": v(364.12, 36) * mm});
            skLineSegment(sketch, "E34.10.6", {"start": v(189.02, -18.38) * mm, "end": v(359.42, 34.53) * mm});
            skLineSegment(sketch, "E34.10.7", {"start": v(322.46, 178.24) * mm, "end": v(362.74, 40.7) * mm});
            skArc(sketch, "E34.10.8", {"start": v(359.42, 34.53) * mm, "mid": v(362.35, 36.94) * mm, "end": v(362.74, 40.7) * mm});
            skLineSegment(sketch, "E34.10.9", {"start": v(161.57, 12.93) * mm, "end": v(189.02, -18.38) * mm});
            skLineSegment(sketch, "E34.10.10", {"start": v(152.57, 29.26) * mm, "end": v(156.8, 24.44) * mm});
            skLineSegment(sketch, "E34.10.11", {"start": v(156.8, 24.44) * mm, "end": v(115.44, -11.82) * mm});
            skLineSegment(sketch, "E34.10.12", {"start": v(123.22, -20.7) * mm, "end": v(161.57, 12.93) * mm});
            skLineSegment(sketch, "E34.10.13", {"start": v(123.22, -20.7) * mm, "end": v(115.44, -11.82) * mm});
            skLineSegment(sketch, "E34.11.0", {"start": v(102.78, 35.2) * mm, "end": v(128.13, 23.52) * mm});
            skLineSegment(sketch, "E34.11.1", {"start": v(125.8, 85.15) * mm, "end": v(102.78, 35.2) * mm});
            skLineSegment(sketch, "E34.11.2", {"start": v(125.8, 85.15) * mm, "end": v(115.1, 90.1) * mm});
            skLineSegment(sketch, "E34.11.3", {"start": v(128.13, 23.52) * mm, "end": v(141.79, 35.5) * mm});
            skLineSegment(sketch, "E34.11.4", {"start": v(127.48, 88.78) * mm, "end": v(222.08, 294) * mm});
            skPoint(sketch, "E34.11.5", {"position": v(318, 180.98) * mm});
            skLineSegment(sketch, "E34.11.6", {"start": v(180.16, 60.1) * mm, "end": v(314.3, 177.74) * mm});
            skLineSegment(sketch, "E34.11.7", {"start": v(222.08, 294) * mm, "end": v(314.82, 184.73) * mm});
            skArc(sketch, "E34.11.8", {"start": v(314.3, 177.74) * mm, "mid": v(316, 181.13) * mm, "end": v(314.82, 184.73) * mm});
            skLineSegment(sketch, "E34.11.9", {"start": v(142.34, 77.53) * mm, "end": v(180.16, 60.1) * mm});
            skLineSegment(sketch, "E34.11.10", {"start": v(127.48, 88.78) * mm, "end": v(133.3, 86.1) * mm});
            skLineSegment(sketch, "E34.11.11", {"start": v(133.3, 86.1) * mm, "end": v(110.27, 36.16) * mm});
            skLineSegment(sketch, "E34.11.12", {"start": v(120.98, 31.22) * mm, "end": v(142.34, 77.53) * mm});
            skLineSegment(sketch, "E34.11.13", {"start": v(120.98, 31.22) * mm, "end": v(110.27, 36.16) * mm});
            skLineSegment(sketch, "E34.12.0", {"start": v(79.58, 73.96) * mm, "end": v(107.49, 73.6) * mm});
            skLineSegment(sketch, "E34.12.1", {"start": v(80.3, 128.96) * mm, "end": v(79.58, 73.96) * mm});
            skLineSegment(sketch, "E34.12.2", {"start": v(80.3, 128.96) * mm, "end": v(68.5, 129.11) * mm});
            skLineSegment(sketch, "E34.12.3", {"start": v(107.49, 73.6) * mm, "end": v(115.1, 90.1) * mm});
            skLineSegment(sketch, "E34.12.4", {"start": v(80.35, 132.96) * mm, "end": v(83.3, 358.9) * mm});
            skPoint(sketch, "E34.12.5", {"position": v(216.9, 294.67) * mm});
            skLineSegment(sketch, "E34.12.6", {"start": v(140.14, 128.18) * mm, "end": v(214.84, 290.21) * mm});
            skLineSegment(sketch, "E34.12.7", {"start": v(83.3, 358.9) * mm, "end": v(212.47, 296.8) * mm});
            skArc(sketch, "E34.12.8", {"start": v(214.84, 290.21) * mm, "mid": v(215, 294) * mm, "end": v(212.47, 296.8) * mm});
            skLineSegment(sketch, "E34.12.9", {"start": v(98.5, 128.72) * mm, "end": v(140.14, 128.18) * mm});
            skLineSegment(sketch, "E34.12.10", {"start": v(80.35, 132.96) * mm, "end": v(86.75, 132.88) * mm});
            skLineSegment(sketch, "E34.12.11", {"start": v(86.75, 132.88) * mm, "end": v(86.03, 77.88) * mm});
            skLineSegment(sketch, "E34.12.12", {"start": v(97.83, 77.73) * mm, "end": v(98.5, 128.72) * mm});
            skLineSegment(sketch, "E34.12.13", {"start": v(97.83, 77.73) * mm, "end": v(86.03, 77.88) * mm});
            skLineSegment(sketch, "E34.13.0", {"start": v(42.61, 99.94) * mm, "end": v(68.26, 110.96) * mm});
            skLineSegment(sketch, "E34.13.1", {"start": v(20.9, 150.47) * mm, "end": v(42.61, 99.94) * mm});
            skLineSegment(sketch, "E34.13.2", {"start": v(20.9, 150.47) * mm, "end": v(10.06, 145.81) * mm});
            skLineSegment(sketch, "E34.13.3", {"start": v(68.26, 110.96) * mm, "end": v(68.5, 129.11) * mm});
            skLineSegment(sketch, "E34.13.4", {"start": v(19.32, 154.15) * mm, "end": v(-69.87, 361.76) * mm});
            skPoint(sketch, "E34.13.5", {"position": v(78.29, 357.42) * mm});
            skLineSegment(sketch, "E34.13.6", {"start": v(75.89, 174.1) * mm, "end": v(78.22, 352.5) * mm});
            skLineSegment(sketch, "E34.13.7", {"start": v(-69.87, 361.76) * mm, "end": v(73.38, 357.57) * mm});
            skArc(sketch, "E34.13.8", {"start": v(78.22, 352.5) * mm, "mid": v(76.84, 356.03) * mm, "end": v(73.38, 357.57) * mm});
            skLineSegment(sketch, "E34.13.9", {"start": v(37.62, 157.66) * mm, "end": v(75.89, 174.1) * mm});
            skLineSegment(sketch, "E34.13.10", {"start": v(19.32, 154.15) * mm, "end": v(25.2, 156.67) * mm});
            skLineSegment(sketch, "E34.13.11", {"start": v(25.2, 156.67) * mm, "end": v(46.91, 106.14) * mm});
            skLineSegment(sketch, "E34.13.12", {"start": v(57.76, 110.8) * mm, "end": v(37.62, 157.66) * mm});
            skLineSegment(sketch, "E34.13.13", {"start": v(57.76, 110.8) * mm, "end": v(46.91, 106.14) * mm});
            skLineSegment(sketch, "E34.14.0", {"start": v(-1.72, 108.63) * mm, "end": v(17.23, 129.13) * mm});
            skLineSegment(sketch, "E34.14.1", {"start": v(-42.1, 145.96) * mm, "end": v(-1.72, 108.63) * mm});
            skLineSegment(sketch, "E34.14.2", {"start": v(-42.1, 145.96) * mm, "end": v(-50.12, 137.3) * mm});
            skLineSegment(sketch, "E34.14.3", {"start": v(17.23, 129.13) * mm, "end": v(10.06, 145.81) * mm});
            skLineSegment(sketch, "E34.14.4", {"start": v(-45.04, 148.68) * mm, "end": v(-210.97, 302.06) * mm});
            skPoint(sketch, "E34.14.5", {"position": v(-73.86, 358.36) * mm});
            skLineSegment(sketch, "E34.14.6", {"start": v(-1.48, 189.9) * mm, "end": v(-71.92, 353.84) * mm});
            skLineSegment(sketch, "E34.14.7", {"start": v(-210.97, 302.06) * mm, "end": v(-78.4, 356.5) * mm});
            skArc(sketch, "E34.14.8", {"start": v(-71.92, 353.84) * mm, "mid": v(-74.62, 356.5) * mm, "end": v(-78.4, 356.5) * mm});
            skLineSegment(sketch, "E34.14.9", {"start": v(-29.75, 159.33) * mm, "end": v(-1.48, 189.9) * mm});
            skLineSegment(sketch, "E34.14.10", {"start": v(-45.04, 148.68) * mm, "end": v(-40.7, 153.38) * mm});
            skLineSegment(sketch, "E34.14.11", {"start": v(-40.7, 153.38) * mm, "end": v(-0.31, 116.04) * mm});
            skLineSegment(sketch, "E34.14.12", {"start": v(7.7, 124.7) * mm, "end": v(-29.75, 159.33) * mm});
            skLineSegment(sketch, "E34.14.13", {"start": v(7.7, 124.7) * mm, "end": v(-0.31, 116.04) * mm});
            skPoint(sketch, "E35", {"position": v(-165.85, 186.8) * mm});
            skPoint(sketch, "E36.1.0", {"position": v(-227.5, 103.2) * mm});
            skPoint(sketch, "E36.2.0", {"position": v(-249.8, 1.75) * mm});
            skPoint(sketch, "E36.3.0", {"position": v(-228.91, -100) * mm});
            skPoint(sketch, "E36.4.0", {"position": v(-168.44, -184.47) * mm});
            skPoint(sketch, "E36.5.0", {"position": v(-78.85, -237.03) * mm});
            skPoint(sketch, "E36.6.0", {"position": v(24.38, -248.61) * mm});
            skPoint(sketch, "E36.7.0", {"position": v(123.39, -217.2) * mm});
            skPoint(sketch, "E36.8.0", {"position": v(201.06, -148.24) * mm});
            skPoint(sketch, "E36.9.0", {"position": v(243.98, -53.64) * mm});
            skPoint(sketch, "E36.10.0", {"position": v(244.7, 50.23) * mm});
            skPoint(sketch, "E36.11.0", {"position": v(203.12, 145.42) * mm});
            skPoint(sketch, "E36.12.0", {"position": v(126.41, 215.46) * mm});
            skPoint(sketch, "E36.13.0", {"position": v(27.85, 248.25) * mm});
            skPoint(sketch, "E36.14.0", {"position": v(-75.53, 238.11) * mm});
            skSolve(sketch);
        }
        {
            var Q0;
            Q0=qCreatedBy(makeId("Top.planeOp"),FACE);
            cPlane(context, id + "F1", {"entities" : qUnion([Q0]), "cplaneType" : CPlaneType.OFFSET, "offset" : 53 * mm, "oppositeDirection" : true, "width" : 150 * mm, "height" : 150 * mm});
        }
        {
            var Q0;
            Q0=qCreatedBy(id+"F1.planeOp",FACE);
            var sketch = newSketch(context, id + "F2", { "sketchPlane" : qUnion([Q0])});
            skPoint(sketch, "E37", {"position": v(0, 0) * mm});
            skPoint(sketch, "E38.2.0", {"position": v(138.9, -207.87) * mm});
            skCircle(sketch, "E38.2.1", {"center": v(153.96, -197.8) * mm, "radius": 1.4 * mm});
            skCircle(sketch, "E38.2.2", {"center": v(123.83, -217.93) * mm, "radius": 1.4 * mm});
            skPoint(sketch, "E38.9.0", {"position": v(-75.53, 238.11) * mm});
            skLineSegment(sketch, "E39", {"start": v(-69.94, 214.6) * mm, "end": v(-55.24, 225) * mm});
            skLineSegment(sketch, "E40", {"start": v(-55.24, 225) * mm, "end": v(-81.79, 262.56) * mm});
            skLineSegment(sketch, "E41", {"start": v(-99.46, 256.38) * mm, "end": v(-69.94, 214.6) * mm});
            skCircle(sketch, "E42", {"center": v(-59.3, 236.81) * mm, "radius": 1.9 * mm});
            skCircle(sketch, "E43", {"center": v(-79.72, 222.38) * mm, "radius": 1.9 * mm});
            skPoint(sketch, "E44.center", {"position": v(0, -0.01) * mm});
            skLineSegment(sketch, "E45.bottom", {"start": v(-15, 22) * mm, "end": v(-10, 22) * mm});
            skLineSegment(sketch, "E45.top", {"start": v(-15, 17) * mm, "end": v(-10, 17) * mm});
            skLineSegment(sketch, "E45.left", {"start": v(-15, 22) * mm, "end": v(-15, 17) * mm});
            skLineSegment(sketch, "E45.right", {"start": v(-10, 22) * mm, "end": v(-10, 17) * mm});
            skLineSegment(sketch, "E46.bottom", {"start": v(10, 22) * mm, "end": v(15, 22) * mm});
            skLineSegment(sketch, "E46.top", {"start": v(10, 17) * mm, "end": v(15, 17) * mm});
            skLineSegment(sketch, "E46.left", {"start": v(10, 22) * mm, "end": v(10, 17) * mm});
            skLineSegment(sketch, "E46.right", {"start": v(15, 22) * mm, "end": v(15, 17) * mm});
            skLineSegment(sketch, "E47.bottom", {"start": v(-15, -17) * mm, "end": v(-10, -17) * mm});
            skLineSegment(sketch, "E47.top", {"start": v(-15, -22) * mm, "end": v(-10, -22) * mm});
            skLineSegment(sketch, "E47.left", {"start": v(-15, -17) * mm, "end": v(-15, -22) * mm});
            skLineSegment(sketch, "E47.right", {"start": v(-10, -17) * mm, "end": v(-10, -22) * mm});
            skLineSegment(sketch, "E48.bottom", {"start": v(10, -17) * mm, "end": v(15, -17) * mm});
            skLineSegment(sketch, "E48.top", {"start": v(10, -22) * mm, "end": v(15, -22) * mm});
            skLineSegment(sketch, "E48.left", {"start": v(10, -17) * mm, "end": v(10, -22) * mm});
            skLineSegment(sketch, "E48.right", {"start": v(15, -17) * mm, "end": v(15, -22) * mm});
            skCircle(sketch, "E49", {"center": v(0, 0) * mm, "radius": 16 * mm});
            skCircle(sketch, "E50", {"center": v(18.3, -55) * mm, "radius": 1.4 * mm});
            skCircle(sketch, "E51.MirrorC", {"center": v(-17.94, -55) * mm, "radius": 1.4 * mm});
            skPoint(sketch, "E52.13.0", {"position": v(0, -55) * mm});
            skLineSegment(sketch, "E53.0", {"start": v(-17.94, -55) * mm, "end": v(18.3, -55) * mm, "construction": true});
            skLineSegment(sketch, "E54.0", {"start": v(-10, -22) * mm, "end": v(15, -22) * mm, "construction": true});
            skLineSegment(sketch, "E55.0", {"start": v(-10, 17) * mm, "end": v(15, 17) * mm, "construction": true});
            skLineSegment(sketch, "E56.0", {"start": v(-10, 22) * mm, "end": v(10, 22) * mm, "construction": true});
            skLineSegment(sketch, "E57.0", {"start": v(-10, -17) * mm, "end": v(10, -17) * mm, "construction": true});
            skLineSegment(sketch, "E58.0", {"start": v(15, -22) * mm, "end": v(15, 17) * mm, "construction": true});
            skLineSegment(sketch, "E59.0", {"start": v(10, -17) * mm, "end": v(10, 17) * mm, "construction": true});
            skLineSegment(sketch, "E60.0", {"start": v(-15, -17) * mm, "end": v(-15, 17) * mm, "construction": true});
            skLineSegment(sketch, "E61.0", {"start": v(-10, -22) * mm, "end": v(-10, 17) * mm, "construction": true});
            skCircle(sketch, "E62.1.0", {"center": v(56.6, 11.96) * mm, "radius": 1.4 * mm});
            skLineSegment(sketch, "E62.1.1", {"start": v(56.6, 11.96) * mm, "end": v(38.49, 43.34) * mm, "construction": true});
            skPoint(sketch, "E62.1.2", {"position": v(47.63, 27.5) * mm});
            skCircle(sketch, "E62.1.3", {"center": v(38.49, 43.34) * mm, "radius": 1.4 * mm});
            skCircle(sketch, "E62.2.0", {"center": v(-38.66, 43.04) * mm, "radius": 1.4 * mm});
            skLineSegment(sketch, "E62.2.1", {"start": v(-38.66, 43.04) * mm, "end": v(-56.78, 11.66) * mm, "construction": true});
            skPoint(sketch, "E62.2.2", {"position": v(-47.63, 27.5) * mm});
            skCircle(sketch, "E62.2.3", {"center": v(-56.78, 11.66) * mm, "radius": 1.4 * mm});
            skArc(sketch, "E63", {"start": v(145.19, 233.55) * mm, "mid": v(34.86, 272.78) * mm, "end": v(-81.79, 262.56) * mm});
            skLineSegment(sketch, "E64", {"start": v(119.48, 150) * mm, "end": v(145.19, 233.55) * mm});
            skLineSegment(sketch, "E65", {"start": v(90, -150) * mm, "end": v(158.96, -191.03) * mm});
            skLineSegment(sketch, "E66", {"start": v(-61.78, 149.9) * mm, "end": v(-61.78, -149.9) * mm});
            skLineSegment(sketch, "E67.left", {"start": v(874.64, -335.26) * mm, "end": v(846.64, -335.26) * mm});
            skLineSegment(sketch, "E67.right", {"start": v(882.69, -279.76) * mm, "end": v(838.59, -279.76) * mm});
            skCircle(sketch, "E68", {"center": v(865.64, -282.76) * mm, "radius": 1.4 * mm});
            skCircle(sketch, "E69", {"center": v(865.64, -330.76) * mm, "radius": 1.4 * mm});
            skLineSegment(sketch, "E70.top", {"start": v(871.64, -286.26) * mm, "end": v(871.64, -327.26) * mm});
            skPoint(sketch, "E71", {"position": v(860.64, -296.76) * mm});
            skCircle(sketch, "E72.MirrorC", {"center": v(855.64, -330.76) * mm, "radius": 1.4 * mm});
            skCircle(sketch, "E73.MirrorC", {"center": v(855.64, -282.76) * mm, "radius": 1.4 * mm});
            skLineSegment(sketch, "E74.MirrorCS", {"start": v(849.64, -286.26) * mm, "end": v(849.64, -327.26) * mm});
            skLineSegment(sketch, "E75", {"start": v(871.64, -327.26) * mm, "end": v(849.64, -327.26) * mm});
            skLineSegment(sketch, "E76", {"start": v(871.64, -286.26) * mm, "end": v(849.64, -286.26) * mm});
            skPoint(sketch, "E77", {"position": v(860.64, -286.26) * mm});
            skLineSegment(sketch, "E78.top", {"start": v(838.59, -301.76) * mm, "end": v(843.59, -301.76) * mm});
            skLineSegment(sketch, "E78.right", {"start": v(843.59, -296.76) * mm, "end": v(843.59, -301.76) * mm});
            skPoint(sketch, "E79", {"position": v(871.64, -306.76) * mm});
            skLineSegment(sketch, "E80", {"start": v(829.64, -261.76) * mm, "end": v(904.33, -261.76) * mm});
            skLineSegment(sketch, "E81.1.0", {"start": v(135.63, 58.7) * mm, "end": v(133.55, 54.04) * mm});
            skLineSegment(sketch, "E81.1.1", {"start": v(129.45, 64.74) * mm, "end": v(139.59, 60.22) * mm});
            skLineSegment(sketch, "E81.1.2", {"start": v(113.34, 28.56) * mm, "end": v(129.45, 64.74) * mm});
            skLineSegment(sketch, "E81.1.3", {"start": v(130.97, 60.77) * mm, "end": v(135.63, 58.7) * mm});
            skLineSegment(sketch, "E81.1.4", {"start": v(130.97, 60.77) * mm, "end": v(128.9, 56.12) * mm});
            skLineSegment(sketch, "E81.1.5", {"start": v(128.9, 56.12) * mm, "end": v(133.55, 54.04) * mm});
            skLineSegment(sketch, "E81.1.6", {"start": v(89.59, 39.13) * mm, "end": v(113.34, 28.56) * mm});
            skLineSegment(sketch, "E81.1.8", {"start": v(97.07, 75.86) * mm, "end": v(95, 71.2) * mm});
            skLineSegment(sketch, "E81.1.9", {"start": v(101.73, 73.8) * mm, "end": v(97.07, 75.86) * mm});
            skLineSegment(sketch, "E81.1.10", {"start": v(99.66, 69.13) * mm, "end": v(95, 71.2) * mm});
            skLineSegment(sketch, "E81.1.11", {"start": v(105.7, 75.31) * mm, "end": v(89.59, 39.13) * mm});
            skLineSegment(sketch, "E81.1.12", {"start": v(101.73, 73.8) * mm, "end": v(99.66, 69.13) * mm});
            skLineSegment(sketch, "E81.2.0", {"start": v(147.78, -1.54) * mm, "end": v(143.99, -4.95) * mm});
            skLineSegment(sketch, "E81.2.1", {"start": v(144.55, 6.46) * mm, "end": v(152.01, -1.76) * mm});
            skLineSegment(sketch, "E81.2.2", {"start": v(115.16, -20) * mm, "end": v(144.55, 6.46) * mm});
            skLineSegment(sketch, "E81.2.3", {"start": v(144.36, 2.25) * mm, "end": v(147.78, -1.54) * mm});
            skLineSegment(sketch, "E81.2.4", {"start": v(144.36, 2.25) * mm, "end": v(140.57, -1.16) * mm});
            skLineSegment(sketch, "E81.2.5", {"start": v(140.57, -1.16) * mm, "end": v(143.99, -4.95) * mm});
            skLineSegment(sketch, "E81.2.6", {"start": v(97.76, -0.69) * mm, "end": v(115.16, -20) * mm});
            skLineSegment(sketch, "E81.2.8", {"start": v(119.54, 29.82) * mm, "end": v(115.75, 26.41) * mm});
            skLineSegment(sketch, "E81.2.9", {"start": v(122.95, 26.03) * mm, "end": v(119.54, 29.82) * mm});
            skLineSegment(sketch, "E81.2.10", {"start": v(119.16, 22.62) * mm, "end": v(115.75, 26.41) * mm});
            skLineSegment(sketch, "E81.2.11", {"start": v(127.19, 25.81) * mm, "end": v(97.76, -0.69) * mm});
            skLineSegment(sketch, "E81.2.12", {"start": v(122.95, 26.03) * mm, "end": v(119.16, 22.62) * mm});
            skLineSegment(sketch, "E81.3.0", {"start": v(134.21, -61.68) * mm, "end": v(129.36, -63.26) * mm});
            skLineSegment(sketch, "E81.3.1", {"start": v(134.65, -52.64) * mm, "end": v(138.15, -63.44) * mm});
            skLineSegment(sketch, "E81.3.2", {"start": v(97.02, -64.86) * mm, "end": v(134.65, -52.64) * mm});
            skLineSegment(sketch, "E81.3.3", {"start": v(132.63, -56.83) * mm, "end": v(134.21, -61.68) * mm});
            skLineSegment(sketch, "E81.3.4", {"start": v(132.63, -56.83) * mm, "end": v(127.78, -58.4) * mm});
            skLineSegment(sketch, "E81.3.5", {"start": v(127.78, -58.4) * mm, "end": v(129.36, -63.26) * mm});
            skLineSegment(sketch, "E81.3.6", {"start": v(89, -40.16) * mm, "end": v(97.02, -64.86) * mm});
            skLineSegment(sketch, "E81.3.8", {"start": v(121.17, -21.55) * mm, "end": v(116.32, -23.12) * mm});
            skLineSegment(sketch, "E81.3.9", {"start": v(122.75, -26.4) * mm, "end": v(121.17, -21.55) * mm});
            skLineSegment(sketch, "E81.3.10", {"start": v(117.9, -27.97) * mm, "end": v(116.32, -23.12) * mm});
            skLineSegment(sketch, "E81.3.11", {"start": v(126.54, -27.95) * mm, "end": v(89, -40.16) * mm});
            skLineSegment(sketch, "E81.3.12", {"start": v(122.75, -26.4) * mm, "end": v(117.9, -27.97) * mm});
            skLineSegment(sketch, "E82", {"start": v(127.19, 25.81) * mm, "end": v(139.59, 60.22) * mm});
            skLineSegment(sketch, "E83", {"start": v(126.54, -27.95) * mm, "end": v(152.01, -1.76) * mm});
            skLineSegment(sketch, "E84", {"start": v(105.7, 170) * mm, "end": v(-61.78, 170) * mm});
            skLineSegment(sketch, "E85", {"start": v(860.64, -286.26) * mm, "end": v(860.64, -329.43) * mm});
            skPoint(sketch, "E85.endSnap0", {"position": v(860.64, -327.26) * mm});
            skLineSegment(sketch, "E86", {"start": v(838.59, -301.76) * mm, "end": v(838.59, -279.76) * mm});
            skLineSegment(sketch, "E87", {"start": v(843.59, -296.76) * mm, "end": v(846.64, -296.76) * mm});
            skLineSegment(sketch, "E88", {"start": v(846.64, -296.76) * mm, "end": v(846.64, -335.26) * mm});
            skLineSegment(sketch, "E89", {"start": v(882.69, -301.76) * mm, "end": v(882.69, -279.76) * mm});
            skLineSegment(sketch, "E90", {"start": v(882.69, -301.76) * mm, "end": v(877.69, -301.76) * mm});
            skLineSegment(sketch, "E91", {"start": v(877.69, -301.76) * mm, "end": v(877.69, -296.76) * mm});
            skLineSegment(sketch, "E92", {"start": v(877.69, -296.76) * mm, "end": v(874.64, -296.76) * mm});
            skLineSegment(sketch, "E93", {"start": v(874.64, -296.76) * mm, "end": v(874.64, -335.26) * mm});
            skLineSegment(sketch, "E94.bottom", {"start": v(502.55, 357.04) * mm, "end": v(452.58, 357.04) * mm});
            skLineSegment(sketch, "E94.top", {"start": v(502.55, 369.04) * mm, "end": v(452.58, 369.04) * mm});
            skPoint(sketch, "E95.visualSharp", {"position": v(447.55, 369.04) * mm});
            skPoint(sketch, "E96.visualSharp", {"position": v(447.55, 357.04) * mm});
            skPoint(sketch, "E97.visualSharp", {"position": v(507.55, 357.04) * mm});
            skPoint(sketch, "E98.visualSharp", {"position": v(507.55, 369.04) * mm});
            skPoint(sketch, "E99", {"position": v(477.55, 363.04) * mm});
            skArc(sketch, "E100", {"start": v(476.13, 364.41) * mm, "mid": v(477.55, 361.06) * mm, "end": v(478.97, 364.41) * mm});
            skLineSegment(sketch, "E101", {"start": v(476.13, 364.41) * mm, "end": v(478.97, 364.41) * mm});
            skPoint(sketch, "E102.middle", {"position": v(543.86, -319.04) * mm});
            skPoint(sketch, "E103", {"position": v(543.86, -327.54) * mm});
            skPoint(sketch, "E104", {"position": v(543.86, -310.54) * mm});
            skCircle(sketch, "E105", {"center": v(543.86, -310.54) * mm, "radius": 2 * mm});
            skCircle(sketch, "E106", {"center": v(543.86, -327.54) * mm, "radius": 2 * mm});
            skCircle(sketch, "E107", {"center": v(543.86, -319.04) * mm, "radius": 5.5 * mm});
            skLineSegment(sketch, "E108.bottom", {"start": v(561.86, -344.04) * mm, "end": v(525.86, -344.04) * mm});
            skLineSegment(sketch, "E108.top", {"start": v(561.86, -294.04) * mm, "end": v(525.86, -294.04) * mm});
            skLineSegment(sketch, "E108.left", {"start": v(561.86, -344.04) * mm, "end": v(561.86, -340.04) * mm});
            skLineSegment(sketch, "E108.right", {"start": v(525.86, -344.04) * mm, "end": v(525.86, -340.04) * mm});
            skLineSegment(sketch, "E109.bottom", {"start": v(528.81, -297.04) * mm, "end": v(533.91, -297.04) * mm});
            skLineSegment(sketch, "E109.top", {"start": v(528.81, -302.14) * mm, "end": v(533.91, -302.14) * mm});
            skLineSegment(sketch, "E109.left", {"start": v(528.81, -297.04) * mm, "end": v(528.81, -302.14) * mm});
            skLineSegment(sketch, "E109.right", {"start": v(533.91, -297.04) * mm, "end": v(533.91, -302.14) * mm});
            skLineSegment(sketch, "E110.bottom", {"start": v(553.81, -297.04) * mm, "end": v(558.91, -297.04) * mm});
            skLineSegment(sketch, "E110.top", {"start": v(553.81, -302.14) * mm, "end": v(558.91, -302.14) * mm});
            skLineSegment(sketch, "E110.left", {"start": v(553.81, -297.04) * mm, "end": v(553.81, -302.14) * mm});
            skLineSegment(sketch, "E110.right", {"start": v(558.91, -297.04) * mm, "end": v(558.91, -302.14) * mm});
            skLineSegment(sketch, "E111.bottom", {"start": v(528.81, -335.94) * mm, "end": v(533.91, -335.94) * mm});
            skLineSegment(sketch, "E111.top", {"start": v(528.81, -341.04) * mm, "end": v(533.91, -341.04) * mm});
            skLineSegment(sketch, "E111.left", {"start": v(528.81, -335.94) * mm, "end": v(528.81, -341.04) * mm});
            skLineSegment(sketch, "E111.right", {"start": v(533.91, -335.94) * mm, "end": v(533.91, -341.04) * mm});
            skLineSegment(sketch, "E112.bottom", {"start": v(553.81, -335.94) * mm, "end": v(558.91, -335.94) * mm});
            skLineSegment(sketch, "E112.top", {"start": v(553.81, -341.04) * mm, "end": v(558.91, -341.04) * mm});
            skLineSegment(sketch, "E112.left", {"start": v(553.81, -335.94) * mm, "end": v(553.81, -341.04) * mm});
            skLineSegment(sketch, "E112.right", {"start": v(558.91, -335.94) * mm, "end": v(558.91, -341.04) * mm});
            skPoint(sketch, "E113", {"position": v(561.86, -319.04) * mm});
            skLineSegment(sketch, "E114", {"start": v(564.86, -312.04) * mm, "end": v(569.86, -312.04) * mm});
            skLineSegment(sketch, "E115", {"start": v(569.86, -312.04) * mm, "end": v(569.86, -317.04) * mm});
            skLineSegment(sketch, "E116", {"start": v(569.86, -317.04) * mm, "end": v(589.86, -317.04) * mm});
            skLineSegment(sketch, "E117", {"start": v(589.86, -317.04) * mm, "end": v(589.86, -312.04) * mm});
            skLineSegment(sketch, "E118", {"start": v(589.86, -312.04) * mm, "end": v(594.86, -312.04) * mm});
            skLineSegment(sketch, "E119", {"start": v(594.86, -312.04) * mm, "end": v(594.86, -317.04) * mm});
            skLineSegment(sketch, "E120", {"start": v(594.86, -317.04) * mm, "end": v(597.86, -317.04) * mm});
            skLineSegment(sketch, "E121", {"start": v(597.86, -317.04) * mm, "end": v(597.86, -340.04) * mm});
            skLineSegment(sketch, "E122", {"start": v(561.86, -340.04) * mm, "end": v(561.86, -317.04) * mm});
            skLineSegment(sketch, "E123", {"start": v(561.86, -317.04) * mm, "end": v(564.86, -317.04) * mm});
            skLineSegment(sketch, "E124", {"start": v(564.86, -317.04) * mm, "end": v(564.86, -312.04) * mm});
            skLineSegment(sketch, "E125", {"start": v(597.86, -340.04) * mm, "end": v(594.86, -340.04) * mm});
            skLineSegment(sketch, "E126", {"start": v(594.86, -340.04) * mm, "end": v(594.86, -345.04) * mm});
            skLineSegment(sketch, "E127", {"start": v(594.86, -345.04) * mm, "end": v(589.86, -345.04) * mm});
            skLineSegment(sketch, "E128", {"start": v(589.86, -345.04) * mm, "end": v(589.86, -340.04) * mm});
            skLineSegment(sketch, "E129", {"start": v(589.86, -340.04) * mm, "end": v(569.86, -340.04) * mm});
            skLineSegment(sketch, "E130", {"start": v(569.86, -340.04) * mm, "end": v(569.86, -345.04) * mm});
            skLineSegment(sketch, "E131", {"start": v(569.86, -345.04) * mm, "end": v(564.86, -345.04) * mm});
            skLineSegment(sketch, "E132", {"start": v(564.86, -345.04) * mm, "end": v(564.86, -340.04) * mm});
            skLineSegment(sketch, "E133", {"start": v(564.86, -340.04) * mm, "end": v(561.86, -340.04) * mm});
            skPoint(sketch, "E134", {"position": v(579.86, -317.04) * mm});
            skLineSegment(sketch, "E135", {"start": v(492.86, -312.04) * mm, "end": v(497.86, -312.04) * mm});
            skLineSegment(sketch, "E136", {"start": v(497.86, -312.04) * mm, "end": v(497.86, -317.04) * mm});
            skLineSegment(sketch, "E137", {"start": v(497.86, -317.04) * mm, "end": v(517.86, -317.04) * mm});
            skLineSegment(sketch, "E138", {"start": v(517.86, -317.04) * mm, "end": v(517.86, -312.04) * mm});
            skLineSegment(sketch, "E139", {"start": v(517.86, -312.04) * mm, "end": v(522.86, -312.04) * mm});
            skLineSegment(sketch, "E140", {"start": v(522.86, -312.04) * mm, "end": v(522.86, -317.04) * mm});
            skLineSegment(sketch, "E141", {"start": v(522.86, -317.04) * mm, "end": v(525.86, -317.04) * mm});
            skLineSegment(sketch, "E142", {"start": v(525.86, -317.04) * mm, "end": v(525.86, -340.04) * mm});
            skLineSegment(sketch, "E143", {"start": v(489.86, -340.04) * mm, "end": v(489.86, -317.04) * mm});
            skLineSegment(sketch, "E144", {"start": v(489.86, -317.04) * mm, "end": v(492.86, -317.04) * mm});
            skLineSegment(sketch, "E145", {"start": v(492.86, -317.04) * mm, "end": v(492.86, -312.04) * mm});
            skLineSegment(sketch, "E146", {"start": v(525.86, -340.04) * mm, "end": v(522.86, -340.04) * mm});
            skLineSegment(sketch, "E147", {"start": v(522.86, -340.04) * mm, "end": v(522.86, -345.04) * mm});
            skLineSegment(sketch, "E148", {"start": v(522.86, -345.04) * mm, "end": v(517.86, -345.04) * mm});
            skLineSegment(sketch, "E149", {"start": v(517.86, -345.04) * mm, "end": v(517.86, -340.04) * mm});
            skLineSegment(sketch, "E150", {"start": v(517.86, -340.04) * mm, "end": v(497.86, -340.04) * mm});
            skLineSegment(sketch, "E151", {"start": v(497.86, -340.04) * mm, "end": v(497.86, -345.04) * mm});
            skLineSegment(sketch, "E152", {"start": v(497.86, -345.04) * mm, "end": v(492.86, -345.04) * mm});
            skLineSegment(sketch, "E153", {"start": v(492.86, -345.04) * mm, "end": v(492.86, -340.04) * mm});
            skLineSegment(sketch, "E154", {"start": v(492.86, -340.04) * mm, "end": v(489.86, -340.04) * mm});
            skPoint(sketch, "E155", {"position": v(507.86, -317.04) * mm});
            skLineSegment(sketch, "E156.trimOffspring", {"start": v(561.86, -317.04) * mm, "end": v(561.86, -294.04) * mm});
            skLineSegment(sketch, "E157.trimOffspring", {"start": v(525.86, -317.04) * mm, "end": v(525.86, -294.04) * mm});
            skLineSegment(sketch, "E158", {"start": v(447.58, 364.05) * mm, "end": v(447.58, 362.05) * mm});
            skLineSegment(sketch, "E159", {"start": v(507.55, 364.04) * mm, "end": v(507.55, 362.04) * mm});
            skArc(sketch, "E160.filletArc", {"start": v(452.58, 369.04) * mm, "mid": v(449.05, 367.58) * mm, "end": v(447.58, 364.05) * mm});
            skPoint(sketch, "E161.newPointA", {"position": v(447.55, 352.22) * mm});
            skArc(sketch, "E161.filletArc", {"start": v(447.58, 362.05) * mm, "mid": v(449.04, 358.5) * mm, "end": v(452.58, 357.04) * mm});
            skArc(sketch, "E162.filletArc", {"start": v(507.55, 364.04) * mm, "mid": v(506.09, 367.57) * mm, "end": v(502.55, 369.04) * mm});
            skArc(sketch, "E163.filletArc", {"start": v(502.55, 357.04) * mm, "mid": v(506.09, 358.5) * mm, "end": v(507.55, 362.04) * mm});
            skLineSegment(sketch, "E164", {"start": v(-174, 175) * mm, "end": v(-174, 212.95) * mm});
            skLineSegment(sketch, "E165", {"start": v(158.96, -224.4) * mm, "end": v(158.96, -191.03) * mm});
            skLineSegment(sketch, "E166", {"start": v(-174, -150) * mm, "end": v(-41.78, -150) * mm});
            skLineSegment(sketch, "E167", {"start": v(-41.78, -150) * mm, "end": v(-61.78, -170) * mm});
            skLineSegment(sketch, "E168", {"start": v(-174, 150) * mm, "end": v(-41.78, 150) * mm});
            skLineSegment(sketch, "E169", {"start": v(-61.78, -170) * mm, "end": v(90, -170) * mm});
            skLineSegment(sketch, "E170", {"start": v(90, -150) * mm, "end": v(77.24, -150) * mm});
            skLineSegment(sketch, "E171", {"start": v(75.12, -155.12) * mm, "end": v(90, -170) * mm});
            skLineSegment(sketch, "E172", {"start": v(-61.78, 170) * mm, "end": v(-41.78, 150) * mm});
            skLineSegment(sketch, "E173", {"start": v(85.7, 150) * mm, "end": v(105.7, 170) * mm});
            skPoint(sketch, "E174.visualSharp", {"position": v(70, -150) * mm});
            skArc(sketch, "E174.filletArc", {"start": v(77.24, -150) * mm, "mid": v(74.47, -151.85) * mm, "end": v(75.12, -155.12) * mm});
            skLineSegment(sketch, "E175", {"start": v(119.48, 150) * mm, "end": v(85.7, 150) * mm});
            skLineSegment(sketch, "E176", {"start": v(-174, 150) * mm, "end": v(-174, 165) * mm});
            skLineSegment(sketch, "E177", {"start": v(-174, -150) * mm, "end": v(-174, -165) * mm});
            skLineSegment(sketch, "E178.1", {"start": v(-61.78, -149.9) * mm, "end": v(-41.54, -149.9) * mm});
            skLineSegment(sketch, "E179.0", {"start": v(90, -149.9) * mm, "end": v(77.24, -149.9) * mm});
            skArc(sketch, "E179.1", {"start": v(77.24, -149.9) * mm, "mid": v(74.4, -151.77) * mm, "end": v(74.99, -155.13) * mm});
            skLineSegment(sketch, "E179.2", {"start": v(74.99, -155.13) * mm, "end": v(89.76, -169.9) * mm});
            skLineSegment(sketch, "E180.0", {"start": v(-41.54, -149.9) * mm, "end": v(-61.54, -169.9) * mm});
            skLineSegment(sketch, "E181.trimOffspring", {"start": v(-61.54, -169.9) * mm, "end": v(89.76, -169.9) * mm});
            skLineSegment(sketch, "E182.0", {"start": v(105.7, 149.9) * mm, "end": v(85.45, 149.9) * mm});
            skLineSegment(sketch, "E182.1", {"start": v(-61.78, 149.9) * mm, "end": v(-41.54, 149.9) * mm});
            skLineSegment(sketch, "E182.2", {"start": v(-61.54, 169.9) * mm, "end": v(-41.54, 149.9) * mm});
            skLineSegment(sketch, "E182.3", {"start": v(105.45, 169.9) * mm, "end": v(-61.54, 169.9) * mm});
            skLineSegment(sketch, "E182.4", {"start": v(85.45, 149.9) * mm, "end": v(105.45, 169.9) * mm});
            skLineSegment(sketch, "E183", {"start": v(-174, -175) * mm, "end": v(-154, -175) * mm});
            skLineSegment(sketch, "E184", {"start": v(-154, -175) * mm, "end": v(-154, -157.72) * mm});
            skLineSegment(sketch, "E185", {"start": v(-154, -157.72) * mm, "end": v(-174, -165) * mm});
            skLineSegment(sketch, "E186", {"start": v(-174, 175) * mm, "end": v(-154, 175) * mm});
            skLineSegment(sketch, "E187", {"start": v(-154, 175) * mm, "end": v(-154, 157.72) * mm});
            skLineSegment(sketch, "E188", {"start": v(-154, 157.72) * mm, "end": v(-174, 165) * mm});
            skLineSegment(sketch, "E189.0", {"start": v(-174.14, 174.8) * mm, "end": v(-212.18, 174.94) * mm});
            skLineSegment(sketch, "E189.1", {"start": v(-174.07, 149.9) * mm, "end": v(-174.11, 165.25) * mm});
            skLineSegment(sketch, "E190.0", {"start": v(-154.2, 158) * mm, "end": v(-174.11, 165.25) * mm});
            skLineSegment(sketch, "E190.1", {"start": v(-154.2, 174.8) * mm, "end": v(-154.2, 158) * mm});
            skLineSegment(sketch, "E190.2", {"start": v(-174.14, 174.8) * mm, "end": v(-154.2, 174.8) * mm});
            skLineSegment(sketch, "E191.0", {"start": v(-174.07, -150.1) * mm, "end": v(-174.07, 149.9) * mm});
            skLineSegment(sketch, "E191.1", {"start": v(-174.07, -150.1) * mm, "end": v(-174.07, -165.24) * mm});
            skLineSegment(sketch, "E192.0", {"start": v(-174, -174.94) * mm, "end": v(-212.18, -174.94) * mm});
            skLineSegment(sketch, "E192.1", {"start": v(-174, -174.94) * mm, "end": v(-154.2, -174.94) * mm});
            skLineSegment(sketch, "E193.0", {"start": v(-154.2, -158) * mm, "end": v(-174.07, -165.24) * mm});
            skLineSegment(sketch, "E193.1", {"start": v(-154.2, -174.94) * mm, "end": v(-154.2, -158) * mm});
            skLineSegment(sketch, "E194.trimOffspring", {"start": v(-174, -175) * mm, "end": v(-174, -212.95) * mm});
            skLineSegment(sketch, "E195.1.0", {"start": v(104.23, -77) * mm, "end": v(138.15, -63.44) * mm});
            skLineSegment(sketch, "E195.1.1", {"start": v(101.93, -68.97) * mm, "end": v(96.86, -68.44) * mm});
            skLineSegment(sketch, "E195.1.2", {"start": v(101.4, -74.04) * mm, "end": v(101.93, -68.97) * mm});
            skLineSegment(sketch, "E195.1.3", {"start": v(104.23, -77) * mm, "end": v(64.97, -72.88) * mm});
            skLineSegment(sketch, "E195.1.4", {"start": v(101.4, -74.04) * mm, "end": v(96.32, -73.5) * mm});
            skLineSegment(sketch, "E195.1.5", {"start": v(96.32, -73.5) * mm, "end": v(96.86, -68.44) * mm});
            skLineSegment(sketch, "E195.1.6", {"start": v(64.97, -72.88) * mm, "end": v(62.25, -98.72) * mm});
            skLineSegment(sketch, "E195.1.7", {"start": v(101.6, -102.85) * mm, "end": v(100.4, -114.15) * mm});
            skLineSegment(sketch, "E195.1.8", {"start": v(62.25, -98.72) * mm, "end": v(101.6, -102.85) * mm});
            skLineSegment(sketch, "E195.1.9", {"start": v(98.05, -105.87) * mm, "end": v(97.52, -110.94) * mm});
            skLineSegment(sketch, "E195.1.10", {"start": v(98.05, -105.87) * mm, "end": v(92.98, -105.33) * mm});
            skLineSegment(sketch, "E195.1.11", {"start": v(92.98, -105.33) * mm, "end": v(92.45, -110.4) * mm});
            skLineSegment(sketch, "E195.1.12", {"start": v(97.52, -110.94) * mm, "end": v(92.45, -110.4) * mm});
            skLineSegment(sketch, "E196", {"start": v(105.7, 75.31) * mm, "end": v(105.7, 149.9) * mm});
            skPoint(sketch, "E197.orphan", {"position": v(105.7, 150) * mm});
            skLineSegment(sketch, "E198", {"start": v(100.4, -114.15) * mm, "end": v(90, -149.9) * mm});
            skLineSegment(sketch, "E199", {"start": v(615.16, -166) * mm, "end": v(615.16, -163) * mm});
            skLineSegment(sketch, "E200.top", {"start": v(615.16, -163) * mm, "end": v(611.66, -163) * mm});
            skLineSegment(sketch, "E200.right", {"start": v(611.66, -166) * mm, "end": v(611.66, -163) * mm});
            skPoint(sketch, "E201", {"position": v(611.66, -166) * mm});
            skLineSegment(sketch, "E202", {"start": v(616.77, -120.1) * mm, "end": v(642.65, -141.8) * mm});
            skLineSegment(sketch, "E203", {"start": v(618.7, -117.8) * mm, "end": v(644.58, -139.5) * mm});
            skPoint(sketch, "E204", {"position": v(621, -119.72) * mm});
            skLineSegment(sketch, "E205", {"start": v(616.77, -120.1) * mm, "end": v(618.7, -117.8) * mm});
            skLineSegment(sketch, "E206", {"start": v(615.16, -166) * mm, "end": v(634.93, -166) * mm});
            skLineSegment(sketch, "E207", {"start": v(615.16, -163) * mm, "end": v(634.93, -163) * mm});
            skLineSegment(sketch, "E208.bottom", {"start": v(615.16, -166) * mm, "end": v(611.66, -166) * mm});
            skArc(sketch, "E209.filletArc", {"start": v(634.93, -163) * mm, "mid": v(646.21, -155.1) * mm, "end": v(642.65, -141.8) * mm});
            skArc(sketch, "E210", {"start": v(634.93, -166) * mm, "mid": v(649.03, -156.13) * mm, "end": v(644.58, -139.5) * mm});
            skPoint(sketch, "E211", {"position": v(640.92, -136.43) * mm});
            skPoint(sketch, "E212", {"position": v(864.13, -283.72) * mm});
            skLineSegment(sketch, "E213", {"start": v(860.27, -282.69) * mm, "end": v(864.35, -267.47) * mm});
            skLineSegment(sketch, "E214", {"start": v(868, -284.76) * mm, "end": v(870.75, -274.47) * mm});
            skLineSegment(sketch, "E215", {"start": v(875.58, -270.76) * mm, "end": v(955.73, -270.76) * mm});
            skArc(sketch, "E216", {"start": v(860.27, -282.69) * mm, "mid": v(863.1, -287.59) * mm, "end": v(868, -284.76) * mm});
            skPoint(sketch, "E217.visualSharp", {"position": v(865.34, -263.76) * mm});
            skArc(sketch, "E217.filletArc", {"start": v(869.18, -263.76) * mm, "mid": v(866.13, -264.8) * mm, "end": v(864.35, -267.47) * mm});
            skPoint(sketch, "E218.visualSharp", {"position": v(871.75, -270.76) * mm});
            skArc(sketch, "E218.filletArc", {"start": v(875.58, -270.76) * mm, "mid": v(872.54, -271.8) * mm, "end": v(870.75, -274.47) * mm});
            skLineSegment(sketch, "E219", {"start": v(955.73, -263.76) * mm, "end": v(955.73, -270.76) * mm});
            skLineSegment(sketch, "E220", {"start": v(864.13, -283.72) * mm, "end": v(860.64, -296.76) * mm});
            skLineSegment(sketch, "E221", {"start": v(864.13, -283.72) * mm, "end": v(866.46, -275.03) * mm});
            skPoint(sketch, "E222", {"position": v(866.46, -275.03) * mm});
            skCircle(sketch, "E223", {"center": v(864.13, -283.72) * mm, "radius": 1.2 * mm});
            skCircle(sketch, "E224", {"center": v(866.46, -275.03) * mm, "radius": 1.2 * mm});
            skLineSegment(sketch, "E225", {"start": v(869.18, -263.76) * mm, "end": v(888.95, -263.76) * mm});
            skLineSegment(sketch, "E226", {"start": v(888.95, -263.76) * mm, "end": v(921.95, -263.76) * mm});
            skLineSegment(sketch, "E227", {"start": v(921.95, -263.76) * mm, "end": v(955.73, -263.76) * mm});
            skPoint(sketch, "E228", {"position": v(905.45, -263.76) * mm});
            skCircle(sketch, "E229", {"center": v(952.73, -267.26) * mm, "radius": 0.95 * mm});
            skPoint(sketch, "E229.centerSnap0", {"position": v(955.73, -267.26) * mm});
            skCircle(sketch, "E230", {"center": v(926.73, -267.26) * mm, "radius": 0.95 * mm});
            skLineSegment(sketch, "E231", {"start": v(116.35, 67.28) * mm, "end": v(124.9, 86.47) * mm});
            skLineSegment(sketch, "E232", {"start": v(128.08, 85.05) * mm, "end": v(129.3, 87.79) * mm});
            skLineSegment(sketch, "E233.top", {"start": v(129.3, 87.79) * mm, "end": v(126.11, 89.2) * mm});
            skLineSegment(sketch, "E233.right", {"start": v(124.9, 86.47) * mm, "end": v(126.11, 89.2) * mm});
            skPoint(sketch, "E234", {"position": v(124.9, 86.47) * mm});
            skLineSegment(sketch, "E235", {"start": v(148.23, 126.32) * mm, "end": v(163.04, 95.97) * mm});
            skLineSegment(sketch, "E236", {"start": v(150.93, 127.64) * mm, "end": v(165.73, 97.28) * mm});
            skPoint(sketch, "E237", {"position": v(152.24, 124.94) * mm});
            skLineSegment(sketch, "E238", {"start": v(148.23, 126.32) * mm, "end": v(150.93, 127.64) * mm});
            skLineSegment(sketch, "E239", {"start": v(128.08, 85.05) * mm, "end": v(146.15, 77) * mm});
            skLineSegment(sketch, "E240", {"start": v(129.3, 87.79) * mm, "end": v(147.37, 79.74) * mm});
            skLineSegment(sketch, "E241.bottom", {"start": v(128.08, 85.05) * mm, "end": v(124.9, 86.47) * mm});
            skArc(sketch, "E242.filletArc", {"start": v(147.37, 79.74) * mm, "mid": v(160.88, 82.37) * mm, "end": v(163.04, 95.97) * mm});
            skArc(sketch, "E243", {"start": v(146.15, 77) * mm, "mid": v(163.04, 80.29) * mm, "end": v(165.73, 97.28) * mm});
            skPoint(sketch, "E244", {"position": v(163.64, 101.57) * mm});
            skLineSegment(sketch, "E245.0", {"start": v(126.11, 89.2) * mm, "end": v(129.3, 87.79) * mm, "construction": true});
            skPoint(sketch, "E246.8.0", {"position": v(121.6, 218.42) * mm});
            skCircle(sketch, "E246.8.1", {"center": v(108.92, 225.47) * mm, "radius": 1.4 * mm});
            skCircle(sketch, "E246.8.2", {"center": v(134.27, 211.38) * mm, "radius": 1.4 * mm});
            skLineSegment(sketch, "E247", {"start": v(108.92, 225.47) * mm, "end": v(134.27, 211.38) * mm});
            skPoint(sketch, "E248.center", {"position": v(326.1, 140.14) * mm});
            skLineSegment(sketch, "E249", {"start": v(105.43, 227.41) * mm, "end": v(137.77, 209.43) * mm});
            skArc(sketch, "E250.trimOffspring", {"start": v(-99.46, 256.38) * mm, "mid": v(-138.45, 237.6) * mm, "end": v(-174, 212.95) * mm});
            skPoint(sketch, "E251", {"position": v(0, 0.02) * mm});
            skPoint(sketch, "E252.8.0", {"position": v(-16.98, 249.43) * mm});
            skCircle(sketch, "E252.8.1", {"center": v(-31.45, 248.43) * mm, "radius": 1.4 * mm});
            skCircle(sketch, "E252.8.2", {"center": v(-2.52, 250.42) * mm, "radius": 1.4 * mm});
            skPoint(sketch, "E253.1.0", {"position": v(54.56, 243.98) * mm});
            skCircle(sketch, "E253.1.1", {"center": v(68.71, 240.82) * mm, "radius": 1.4 * mm});
            skCircle(sketch, "E253.1.2", {"center": v(40.4, 247.13) * mm, "radius": 1.4 * mm});
            skLineSegment(sketch, "E253.anchor1", {"start": v(0, 0) * mm, "end": v(-31.45, 248.43) * mm, "construction": true});
            skLineSegment(sketch, "E253.anchor2", {"start": v(0, 0) * mm, "end": v(40.4, 247.13) * mm, "construction": true});
            skPoint(sketch, "E254.1.0", {"position": v(76.22, -238.1) * mm});
            skCircle(sketch, "E254.1.1", {"center": v(58.96, -243.62) * mm, "radius": 1.4 * mm});
            skCircle(sketch, "E254.1.2", {"center": v(93.47, -232.58) * mm, "radius": 1.4 * mm});
            skPoint(sketch, "E254.2.0", {"position": v(7.63, -249.88) * mm});
            skCircle(sketch, "E254.2.1", {"center": v(-10.47, -250.44) * mm, "radius": 1.4 * mm});
            skCircle(sketch, "E254.2.2", {"center": v(25.74, -249.33) * mm, "radius": 1.4 * mm});
            skPoint(sketch, "E254.3.0", {"position": v(-61.54, -242.3) * mm});
            skCircle(sketch, "E254.3.1", {"center": v(-79.1, -237.85) * mm, "radius": 1.4 * mm});
            skCircle(sketch, "E254.3.2", {"center": v(-43.98, -246.77) * mm, "radius": 1.4 * mm});
            skPoint(sketch, "E254.4.0", {"position": v(-125.94, -215.96) * mm});
            skCircle(sketch, "E254.4.1", {"center": v(-141.6, -206.83) * mm, "radius": 1.4 * mm});
            skCircle(sketch, "E254.4.2", {"center": v(-110.3, -225.09) * mm, "radius": 1.4 * mm});
            skPoint(sketch, "E254.5.0", {"position": v(-180.6, -172.88) * mm});
            skCircle(sketch, "E254.5.1", {"center": v(-193.12, -159.8) * mm, "radius": 1.4 * mm});
            skCircle(sketch, "E254.5.2", {"center": v(-168.06, -185.97) * mm, "radius": 1.4 * mm});
            skPoint(sketch, "E254.6.0", {"position": v(-221.25, -116.4) * mm});
            skCircle(sketch, "E254.6.1", {"center": v(-229.68, -100.37) * mm, "radius": 1.4 * mm});
            skCircle(sketch, "E254.6.2", {"center": v(-212.81, -132.44) * mm, "radius": 1.4 * mm});
            skPoint(sketch, "E254.7.0", {"position": v(-244.76, -50.91) * mm});
            skCircle(sketch, "E254.7.1", {"center": v(-248.45, -33.17) * mm, "radius": 1.4 * mm});
            skCircle(sketch, "E254.7.2", {"center": v(-241.07, -68.65) * mm, "radius": 1.4 * mm});
            skPoint(sketch, "E254.8.0", {"position": v(-249.31, 18.53) * mm});
            skCircle(sketch, "E254.8.1", {"center": v(-247.97, 36.6) * mm, "radius": 1.4 * mm});
            skCircle(sketch, "E254.8.2", {"center": v(-250.66, 0.46) * mm, "radius": 1.4 * mm});
            skPoint(sketch, "E254.9.0", {"position": v(-234.55, 86.53) * mm});
            skCircle(sketch, "E254.9.1", {"center": v(-228.28, 103.53) * mm, "radius": 1.4 * mm});
            skCircle(sketch, "E254.9.2", {"center": v(-240.82, 69.53) * mm, "radius": 1.4 * mm});
            skPoint(sketch, "E254.10.0", {"position": v(-201.61, 147.83) * mm});
            skCircle(sketch, "E254.10.1", {"center": v(-190.9, 162.44) * mm, "radius": 1.4 * mm});
            skCircle(sketch, "E254.10.2", {"center": v(-212.32, 133.22) * mm, "radius": 1.4 * mm});
            skPoint(sketch, "E254.11.0", {"position": v(-153.05, 197.67) * mm});
            skCircle(sketch, "E254.11.1", {"center": v(-138.73, 208.76) * mm, "radius": 1.4 * mm});
            skCircle(sketch, "E254.11.2", {"center": v(-167.38, 186.58) * mm, "radius": 1.4 * mm});
            skLineSegment(sketch, "E254.anchor1", {"start": v(0, 0) * mm, "end": v(123.83, -217.93) * mm, "construction": true});
            skLineSegment(sketch, "E254.anchor2", {"start": v(0, 0) * mm, "end": v(-138.73, 208.76) * mm, "construction": true});
            skArc(sketch, "E255.trimOffspring", {"start": v(-212.18, 174.94) * mm, "mid": v(-275, 0) * mm, "end": v(-212.18, -174.94) * mm});
            skArc(sketch, "E256.trimOffspring", {"start": v(-174, -212.95) * mm, "mid": v(-9.45, -274.84) * mm, "end": v(158.96, -224.4) * mm});
            skSolve(sketch);
        }
        {
            var Q0;
            Q0=qCreatedBy(makeId("Top.planeOp"),FACE);
            cPlane(context, id + "F3", {"entities" : qUnion([Q0]), "cplaneType" : CPlaneType.OFFSET, "offset" : 180 * mm, "oppositeDirection" : true, "width" : 150 * mm, "height" : 150 * mm});
        }
        {
            var Q0;
            Q0=qCreatedBy(id+"F3.planeOp",FACE);
            var sketch = newSketch(context, id + "F4", { "sketchPlane" : qUnion([Q0])});
            skLineSegment(sketch, "E257.8.0", {"start": v(150, -96.9) * mm, "end": v(430.96, -130.16) * mm});
            skLineSegment(sketch, "E257.8.1", {"start": v(150, -174.88) * mm, "end": v(356.74, -297.88) * mm});
            skLineSegment(sketch, "E257.9.0", {"start": v(150, -35.73) * mm, "end": v(441.48, 54.78) * mm});
            skLineSegment(sketch, "E257.9.1", {"start": v(150, -91.87) * mm, "end": v(432.12, -125.26) * mm});
            skLineSegment(sketch, "E257.10.0", {"start": v(150, 27) * mm, "end": v(385.03, 233.12) * mm});
            skLineSegment(sketch, "E257.10.1", {"start": v(150, -30.5) * mm, "end": v(440.82, 59.81) * mm});
            skLineSegment(sketch, "E257.11.0", {"start": v(150, 153.59) * mm, "end": v(258.23, 388.35) * mm});
            skLineSegment(sketch, "E257.11.1", {"start": v(150, 33.65) * mm, "end": v(382.6, 237.63) * mm});
            skArc(sketch, "E258", {"start": v(356.74, -297.88) * mm, "mid": v(440.2, 64.29) * mm, "end": v(258.23, 388.35) * mm});
            skLineSegment(sketch, "E259", {"start": v(254.24, 391.65) * mm, "end": v(129.21, 120.44) * mm});
            skLineSegment(sketch, "E260", {"start": v(113.89, -159.22) * mm, "end": v(354.18, -302.18) * mm});
            skLineSegment(sketch, "E261", {"start": v(258.23, 388.35) * mm, "end": v(254.24, 391.65) * mm});
            skLineSegment(sketch, "E262", {"start": v(356.74, -297.88) * mm, "end": v(354.18, -302.18) * mm});
            skArc(sketch, "E263", {"start": v(113.89, -159.22) * mm, "mid": v(167.22, -21.9) * mm, "end": v(129.21, 120.44) * mm});
            skPoint(sketch, "E264", {"position": v(0, 0) * mm});
            skSolve(sketch);
        }
        {
            var Q0;
            Q0=qSketchRegion(id+"F4",true);
            extrude(context, id + "F5", {"entities" : qUnion([Q0]), "oppositeDirection" : true, "depth" : 40 * mm});
        }
        {
            var Q0;
            {var subQ0=sQuery(id+"F4.wireOp",EDGE,"E258");var subQ1=sQuery(id+"F4.wireOp",EDGE,"E257.8.0");var subQ2=makeQuery(id+"F4.imprint","INTERSECT",VERTEX,{"derivedFrom":[subQ1,subQ0]});Q0=makeQuery(id+"F4.imprint","IMPRINT",FACE,{"disambiguationData":[TD([[makeQuery(id+"F4.imprint","IMPRINT",EDGE,{"disambiguationData":[TD([[subQ2,1.0]])],"derivedFrom":subQ1}),-1.0]])]});}
            var Q1;
            {var subQ0=sQuery(id+"F4.wireOp",EDGE,"E258");var subQ1=sQuery(id+"F4.wireOp",EDGE,"E257.9.0");var subQ2=makeQuery(id+"F4.imprint","INTERSECT",VERTEX,{"derivedFrom":[subQ1,subQ0]});Q1=makeQuery(id+"F4.imprint","IMPRINT",FACE,{"disambiguationData":[TD([[makeQuery(id+"F4.imprint","IMPRINT",EDGE,{"disambiguationData":[TD([[subQ2,1.0]])],"derivedFrom":subQ1}),-1.0]])]});}
            var Q2;
            {var subQ0=sQuery(id+"F4.wireOp",EDGE,"E258");var subQ1=sQuery(id+"F4.wireOp",EDGE,"E257.10.0");var subQ2=makeQuery(id+"F4.imprint","INTERSECT",VERTEX,{"derivedFrom":[subQ1,subQ0]});Q2=makeQuery(id+"F4.imprint","IMPRINT",FACE,{"disambiguationData":[TD([[makeQuery(id+"F4.imprint","IMPRINT",EDGE,{"disambiguationData":[TD([[subQ2,1.0]])],"derivedFrom":subQ1}),-1.0]])]});}
            var Q3;
            {var subQ0=sQuery(id+"F4.wireOp",EDGE,"E258");var subQ5=sQuery(id+"F4.wireOp",EDGE,"E257.11.1");var subQ7=makeQuery(id+"F4.imprint","INTERSECT",VERTEX,{"derivedFrom":[subQ5,subQ0]});Q3=makeQuery(id+"F4.imprint","IMPRINT",FACE,{"disambiguationData":[TD([[makeQuery(id+"F4.imprint","IMPRINT",EDGE,{"disambiguationData":[TD([[subQ7,1.0]])],"derivedFrom":subQ5}),1.0]])]});}
            extrude(context, id + "F6", {"entities" : qUnion([Q0, Q1, Q2, Q3]), "operationType" : NewBodyOperationType.REMOVE, "oppositeDirection" : true, "depth" : 35 * mm});
        }
        {
            var Q0;
            Q0=makeQuery(id+"F6.boolean.opBoolean","COPY",EDGE,{"derivedFrom":makeQuery(id+"F6.opExtrude","CAP_EDGE",EDGE,{"disambiguationData":[OSD([sQuery(id+"F4.wireOp",EDGE,"E257.8.0")])],"isStart":false})});
            var Q1;
            Q1=makeQuery(id+"F6.boolean.opBoolean","COPY",EDGE,{"derivedFrom":makeQuery(id+"F6.opExtrude","CAP_EDGE",EDGE,{"disambiguationData":[OSD([sQuery(id+"F4.wireOp",EDGE,"E257.9.0")])],"isStart":false})});
            var Q2;
            Q2=makeQuery(id+"F6.boolean.opBoolean","COPY",EDGE,{"derivedFrom":makeQuery(id+"F6.opExtrude","CAP_EDGE",EDGE,{"disambiguationData":[OSD([sQuery(id+"F4.wireOp",EDGE,"E257.10.0")])],"isStart":false})});
            var Q3;
            Q3=makeQuery(id+"F6.boolean.opBoolean","COPY",EDGE,{"derivedFrom":makeQuery(id+"F6.opExtrude","CAP_EDGE",EDGE,{"disambiguationData":[OSD([sQuery(id+"F4.wireOp",EDGE,"E257.11.0")])],"isStart":false})});
            var Q4;
            Q4=makeQuery(id+"F6.boolean.opBoolean","COPY",EDGE,{"derivedFrom":makeQuery(id+"F6.opExtrude","CAP_EDGE",EDGE,{"disambiguationData":[OSD([sQuery(id+"F4.wireOp",EDGE,"E257.8.1")])],"isStart":false})});
            var Q5;
            Q5=makeQuery(id+"F6.boolean.opBoolean","COPY",EDGE,{"derivedFrom":makeQuery(id+"F6.opExtrude","CAP_EDGE",EDGE,{"disambiguationData":[OSD([sQuery(id+"F4.wireOp",EDGE,"E257.9.1")])],"isStart":false})});
            var Q6;
            Q6=makeQuery(id+"F6.boolean.opBoolean","COPY",EDGE,{"derivedFrom":makeQuery(id+"F6.opExtrude","CAP_EDGE",EDGE,{"disambiguationData":[OSD([sQuery(id+"F4.wireOp",EDGE,"E257.10.1")])],"isStart":false})});
            var Q7;
            Q7=makeQuery(id+"F6.boolean.opBoolean","COPY",EDGE,{"derivedFrom":makeQuery(id+"F6.opExtrude","CAP_EDGE",EDGE,{"disambiguationData":[OSD([sQuery(id+"F4.wireOp",EDGE,"E257.11.1")])],"isStart":false})});
            fillet(context, id + "F7", {"entities" : qUnion([Q0, Q1, Q2, Q3, Q4, Q5, Q6, Q7]), "radius" : 20 * mm, "tangentPropagation" : true, "allowEdgeOverflow" : false});
        }
        {
            var Q0;
            Q0=makeQuery(id+"F0.imprint","IMPRINT",FACE,{"disambiguationData":[TD([[makeQuery(id+"F0.imprint","IMPRINT",EDGE,{"derivedFrom":sQuery(id+"F0.wireOp",EDGE,"E1")}),1.0]])]});
            var Q1;
            Q1=makeQuery(id+"F0.imprint","IMPRINT",FACE,{"disambiguationData":[TD([[makeQuery(id+"F0.imprint","IMPRINT",EDGE,{"derivedFrom":sQuery(id+"F0.wireOp",EDGE,"E34.1.4")}),-1.0]])]});
            var Q2;
            Q2=makeQuery(id+"F0.imprint","IMPRINT",FACE,{"disambiguationData":[TD([[makeQuery(id+"F0.imprint","IMPRINT",EDGE,{"derivedFrom":sQuery(id+"F0.wireOp",EDGE,"E34.2.4")}),-1.0]])]});
            var Q3;
            Q3=makeQuery(id+"F0.imprint","IMPRINT",FACE,{"disambiguationData":[TD([[makeQuery(id+"F0.imprint","IMPRINT",EDGE,{"derivedFrom":sQuery(id+"F0.wireOp",EDGE,"E34.3.4")}),-1.0]])]});
            var Q4;
            Q4=makeQuery(id+"F0.imprint","IMPRINT",FACE,{"disambiguationData":[TD([[makeQuery(id+"F0.imprint","IMPRINT",EDGE,{"derivedFrom":sQuery(id+"F0.wireOp",EDGE,"E34.4.4")}),-1.0]])]});
            var Q5;
            Q5=makeQuery(id+"F0.imprint","IMPRINT",FACE,{"disambiguationData":[TD([[makeQuery(id+"F0.imprint","IMPRINT",EDGE,{"derivedFrom":sQuery(id+"F0.wireOp",EDGE,"E34.5.4")}),-1.0]])]});
            var Q6;
            Q6=makeQuery(id+"F0.imprint","IMPRINT",FACE,{"disambiguationData":[TD([[makeQuery(id+"F0.imprint","IMPRINT",EDGE,{"derivedFrom":sQuery(id+"F0.wireOp",EDGE,"E34.6.4")}),-1.0]])]});
            var Q7;
            Q7=makeQuery(id+"F0.imprint","IMPRINT",FACE,{"disambiguationData":[TD([[makeQuery(id+"F0.imprint","IMPRINT",EDGE,{"derivedFrom":sQuery(id+"F0.wireOp",EDGE,"E34.7.4")}),-1.0]])]});
            var Q8;
            Q8=makeQuery(id+"F0.imprint","IMPRINT",FACE,{"disambiguationData":[TD([[makeQuery(id+"F0.imprint","IMPRINT",EDGE,{"derivedFrom":sQuery(id+"F0.wireOp",EDGE,"E34.8.4")}),-1.0]])]});
            var Q9;
            Q9=makeQuery(id+"F0.imprint","IMPRINT",FACE,{"disambiguationData":[TD([[makeQuery(id+"F0.imprint","IMPRINT",EDGE,{"derivedFrom":sQuery(id+"F0.wireOp",EDGE,"E34.9.4")}),-1.0]])]});
            var Q10;
            Q10=makeQuery(id+"F0.imprint","IMPRINT",FACE,{"disambiguationData":[TD([[makeQuery(id+"F0.imprint","IMPRINT",EDGE,{"derivedFrom":sQuery(id+"F0.wireOp",EDGE,"E34.10.4")}),-1.0]])]});
            var Q11;
            Q11=makeQuery(id+"F0.imprint","IMPRINT",FACE,{"disambiguationData":[TD([[makeQuery(id+"F0.imprint","IMPRINT",EDGE,{"derivedFrom":sQuery(id+"F0.wireOp",EDGE,"E34.11.4")}),-1.0]])]});
            var Q12;
            Q12=makeQuery(id+"F0.imprint","IMPRINT",FACE,{"disambiguationData":[TD([[makeQuery(id+"F0.imprint","IMPRINT",EDGE,{"derivedFrom":sQuery(id+"F0.wireOp",EDGE,"E34.12.4")}),-1.0]])]});
            var Q13;
            Q13=makeQuery(id+"F0.imprint","IMPRINT",FACE,{"disambiguationData":[TD([[makeQuery(id+"F0.imprint","IMPRINT",EDGE,{"derivedFrom":sQuery(id+"F0.wireOp",EDGE,"E34.13.4")}),-1.0]])]});
            var Q14;
            Q14=makeQuery(id+"F0.imprint","IMPRINT",FACE,{"disambiguationData":[TD([[makeQuery(id+"F0.imprint","IMPRINT",EDGE,{"derivedFrom":sQuery(id+"F0.wireOp",EDGE,"E34.14.4")}),-1.0]])]});
            var Q15;
            {var subQ0=sQuery(id+"F0.wireOp",EDGE,"E18.left");Q15=makeQuery(id+"F0.imprint","IMPRINT",FACE,{"disambiguationData":[TD([[makeQuery(id+"F0.imprint","IMPRINT",EDGE,{"derivedFrom":subQ0}),1.0]])]});}
            var Q16;
            {var subQ0=sQuery(id+"F0.wireOp",EDGE,"E18.right");Q16=makeQuery(id+"F0.imprint","IMPRINT",FACE,{"disambiguationData":[TD([[makeQuery(id+"F0.imprint","IMPRINT",EDGE,{"derivedFrom":subQ0}),1.0]])]});}
            var Q17;
            {var subQ0=sQuery(id+"F0.wireOp",EDGE,"E26.1.16");Q17=makeQuery(id+"F0.imprint","IMPRINT",FACE,{"disambiguationData":[TD([[makeQuery(id+"F0.imprint","IMPRINT",EDGE,{"derivedFrom":subQ0}),1.0]])]});}
            var Q18;
            {var subQ0=sQuery(id+"F0.wireOp",EDGE,"E26.1.17");Q18=makeQuery(id+"F0.imprint","IMPRINT",FACE,{"disambiguationData":[TD([[makeQuery(id+"F0.imprint","IMPRINT",EDGE,{"derivedFrom":subQ0}),1.0]])]});}
            var Q19;
            {var subQ0=sQuery(id+"F0.wireOp",EDGE,"E26.2.16");Q19=makeQuery(id+"F0.imprint","IMPRINT",FACE,{"disambiguationData":[TD([[makeQuery(id+"F0.imprint","IMPRINT",EDGE,{"derivedFrom":subQ0}),1.0]])]});}
            var Q20;
            {var subQ0=sQuery(id+"F0.wireOp",EDGE,"E26.2.17");Q20=makeQuery(id+"F0.imprint","IMPRINT",FACE,{"disambiguationData":[TD([[makeQuery(id+"F0.imprint","IMPRINT",EDGE,{"derivedFrom":subQ0}),1.0]])]});}
            var Q21;
            {var subQ0=sQuery(id+"F0.wireOp",EDGE,"E26.3.16");Q21=makeQuery(id+"F0.imprint","IMPRINT",FACE,{"disambiguationData":[TD([[makeQuery(id+"F0.imprint","IMPRINT",EDGE,{"derivedFrom":subQ0}),1.0]])]});}
            var Q22;
            {var subQ0=sQuery(id+"F0.wireOp",EDGE,"E26.3.17");Q22=makeQuery(id+"F0.imprint","IMPRINT",FACE,{"disambiguationData":[TD([[makeQuery(id+"F0.imprint","IMPRINT",EDGE,{"derivedFrom":subQ0}),1.0]])]});}
            var Q23;
            {var subQ0=sQuery(id+"F0.wireOp",EDGE,"E26.4.16");Q23=makeQuery(id+"F0.imprint","IMPRINT",FACE,{"disambiguationData":[TD([[makeQuery(id+"F0.imprint","IMPRINT",EDGE,{"derivedFrom":subQ0}),1.0]])]});}
            var Q24;
            {var subQ0=sQuery(id+"F0.wireOp",EDGE,"E26.4.17");Q24=makeQuery(id+"F0.imprint","IMPRINT",FACE,{"disambiguationData":[TD([[makeQuery(id+"F0.imprint","IMPRINT",EDGE,{"derivedFrom":subQ0}),1.0]])]});}
            var Q25;
            {var subQ0=sQuery(id+"F0.wireOp",EDGE,"E26.5.16");Q25=makeQuery(id+"F0.imprint","IMPRINT",FACE,{"disambiguationData":[TD([[makeQuery(id+"F0.imprint","IMPRINT",EDGE,{"derivedFrom":subQ0}),1.0]])]});}
            var Q26;
            {var subQ0=sQuery(id+"F0.wireOp",EDGE,"E26.5.17");Q26=makeQuery(id+"F0.imprint","IMPRINT",FACE,{"disambiguationData":[TD([[makeQuery(id+"F0.imprint","IMPRINT",EDGE,{"derivedFrom":subQ0}),1.0]])]});}
            var Q27;
            {var subQ0=sQuery(id+"F0.wireOp",EDGE,"E26.6.16");Q27=makeQuery(id+"F0.imprint","IMPRINT",FACE,{"disambiguationData":[TD([[makeQuery(id+"F0.imprint","IMPRINT",EDGE,{"derivedFrom":subQ0}),1.0]])]});}
            var Q28;
            {var subQ0=sQuery(id+"F0.wireOp",EDGE,"E26.6.17");Q28=makeQuery(id+"F0.imprint","IMPRINT",FACE,{"disambiguationData":[TD([[makeQuery(id+"F0.imprint","IMPRINT",EDGE,{"derivedFrom":subQ0}),1.0]])]});}
            var Q29;
            {var subQ0=sQuery(id+"F0.wireOp",EDGE,"E26.7.16");Q29=makeQuery(id+"F0.imprint","IMPRINT",FACE,{"disambiguationData":[TD([[makeQuery(id+"F0.imprint","IMPRINT",EDGE,{"derivedFrom":subQ0}),1.0]])]});}
            var Q30;
            {var subQ0=sQuery(id+"F0.wireOp",EDGE,"E26.7.17");Q30=makeQuery(id+"F0.imprint","IMPRINT",FACE,{"disambiguationData":[TD([[makeQuery(id+"F0.imprint","IMPRINT",EDGE,{"derivedFrom":subQ0}),1.0]])]});}
            var Q31;
            {var subQ0=sQuery(id+"F0.wireOp",EDGE,"E26.8.16");Q31=makeQuery(id+"F0.imprint","IMPRINT",FACE,{"disambiguationData":[TD([[makeQuery(id+"F0.imprint","IMPRINT",EDGE,{"derivedFrom":subQ0}),1.0]])]});}
            var Q32;
            {var subQ0=sQuery(id+"F0.wireOp",EDGE,"E26.8.17");Q32=makeQuery(id+"F0.imprint","IMPRINT",FACE,{"disambiguationData":[TD([[makeQuery(id+"F0.imprint","IMPRINT",EDGE,{"derivedFrom":subQ0}),1.0]])]});}
            var Q33;
            {var subQ0=sQuery(id+"F0.wireOp",EDGE,"E26.9.16");Q33=makeQuery(id+"F0.imprint","IMPRINT",FACE,{"disambiguationData":[TD([[makeQuery(id+"F0.imprint","IMPRINT",EDGE,{"derivedFrom":subQ0}),1.0]])]});}
            var Q34;
            {var subQ0=sQuery(id+"F0.wireOp",EDGE,"E26.9.17");Q34=makeQuery(id+"F0.imprint","IMPRINT",FACE,{"disambiguationData":[TD([[makeQuery(id+"F0.imprint","IMPRINT",EDGE,{"derivedFrom":subQ0}),1.0]])]});}
            var Q35;
            {var subQ0=sQuery(id+"F0.wireOp",EDGE,"E26.10.16");Q35=makeQuery(id+"F0.imprint","IMPRINT",FACE,{"disambiguationData":[TD([[makeQuery(id+"F0.imprint","IMPRINT",EDGE,{"derivedFrom":subQ0}),1.0]])]});}
            var Q36;
            {var subQ0=sQuery(id+"F0.wireOp",EDGE,"E26.10.17");Q36=makeQuery(id+"F0.imprint","IMPRINT",FACE,{"disambiguationData":[TD([[makeQuery(id+"F0.imprint","IMPRINT",EDGE,{"derivedFrom":subQ0}),1.0]])]});}
            var Q37;
            {var subQ0=sQuery(id+"F0.wireOp",EDGE,"E26.11.16");Q37=makeQuery(id+"F0.imprint","IMPRINT",FACE,{"disambiguationData":[TD([[makeQuery(id+"F0.imprint","IMPRINT",EDGE,{"derivedFrom":subQ0}),1.0]])]});}
            var Q38;
            {var subQ0=sQuery(id+"F0.wireOp",EDGE,"E26.11.17");Q38=makeQuery(id+"F0.imprint","IMPRINT",FACE,{"disambiguationData":[TD([[makeQuery(id+"F0.imprint","IMPRINT",EDGE,{"derivedFrom":subQ0}),1.0]])]});}
            var Q39;
            {var subQ0=sQuery(id+"F0.wireOp",EDGE,"E26.12.16");Q39=makeQuery(id+"F0.imprint","IMPRINT",FACE,{"disambiguationData":[TD([[makeQuery(id+"F0.imprint","IMPRINT",EDGE,{"derivedFrom":subQ0}),1.0]])]});}
            var Q40;
            {var subQ0=sQuery(id+"F0.wireOp",EDGE,"E26.12.17");Q40=makeQuery(id+"F0.imprint","IMPRINT",FACE,{"disambiguationData":[TD([[makeQuery(id+"F0.imprint","IMPRINT",EDGE,{"derivedFrom":subQ0}),1.0]])]});}
            var Q41;
            {var subQ0=sQuery(id+"F0.wireOp",EDGE,"E26.13.16");Q41=makeQuery(id+"F0.imprint","IMPRINT",FACE,{"disambiguationData":[TD([[makeQuery(id+"F0.imprint","IMPRINT",EDGE,{"derivedFrom":subQ0}),1.0]])]});}
            var Q42;
            {var subQ0=sQuery(id+"F0.wireOp",EDGE,"E26.13.17");Q42=makeQuery(id+"F0.imprint","IMPRINT",FACE,{"disambiguationData":[TD([[makeQuery(id+"F0.imprint","IMPRINT",EDGE,{"derivedFrom":subQ0}),1.0]])]});}
            var Q43;
            {var subQ0=sQuery(id+"F0.wireOp",EDGE,"E26.14.16");Q43=makeQuery(id+"F0.imprint","IMPRINT",FACE,{"disambiguationData":[TD([[makeQuery(id+"F0.imprint","IMPRINT",EDGE,{"derivedFrom":subQ0}),1.0]])]});}
            var Q44;
            {var subQ0=sQuery(id+"F0.wireOp",EDGE,"E26.14.17");Q44=makeQuery(id+"F0.imprint","IMPRINT",FACE,{"disambiguationData":[TD([[makeQuery(id+"F0.imprint","IMPRINT",EDGE,{"derivedFrom":subQ0}),1.0]])]});}
            var Q45;
            {var subQ0=sQuery(id+"F0.wireOp",EDGE,"E12.left");Q45=makeQuery(id+"F0.imprint","IMPRINT",FACE,{"disambiguationData":[TD([[makeQuery(id+"F0.imprint","IMPRINT",EDGE,{"derivedFrom":subQ0}),1.0]])]});}
            var Q46;
            {var subQ0=sQuery(id+"F0.wireOp",EDGE,"E12.right");Q46=makeQuery(id+"F0.imprint","IMPRINT",FACE,{"disambiguationData":[TD([[makeQuery(id+"F0.imprint","IMPRINT",EDGE,{"derivedFrom":subQ0}),-1.0]])]});}
            var Q47;
            Q47=makeQuery(id+"F0.imprint","IMPRINT",FACE,{"disambiguationData":[TD([[makeQuery(id+"F0.imprint","IMPRINT",EDGE,{"derivedFrom":sQuery(id+"F0.wireOp",EDGE,"E26.1.0")}),-1.0]])]});
            var Q48;
            Q48=makeQuery(id+"F0.imprint","IMPRINT",FACE,{"disambiguationData":[TD([[makeQuery(id+"F0.imprint","IMPRINT",EDGE,{"derivedFrom":sQuery(id+"F0.wireOp",EDGE,"E26.1.4")}),-1.0]])]});
            var Q49;
            Q49=makeQuery(id+"F0.imprint","IMPRINT",FACE,{"disambiguationData":[TD([[makeQuery(id+"F0.imprint","IMPRINT",EDGE,{"derivedFrom":sQuery(id+"F0.wireOp",EDGE,"E26.2.0")}),-1.0]])]});
            var Q50;
            Q50=makeQuery(id+"F0.imprint","IMPRINT",FACE,{"disambiguationData":[TD([[makeQuery(id+"F0.imprint","IMPRINT",EDGE,{"derivedFrom":sQuery(id+"F0.wireOp",EDGE,"E26.2.4")}),-1.0]])]});
            var Q51;
            Q51=makeQuery(id+"F0.imprint","IMPRINT",FACE,{"disambiguationData":[TD([[makeQuery(id+"F0.imprint","IMPRINT",EDGE,{"derivedFrom":sQuery(id+"F0.wireOp",EDGE,"E26.3.0")}),-1.0]])]});
            var Q52;
            Q52=makeQuery(id+"F0.imprint","IMPRINT",FACE,{"disambiguationData":[TD([[makeQuery(id+"F0.imprint","IMPRINT",EDGE,{"derivedFrom":sQuery(id+"F0.wireOp",EDGE,"E26.3.4")}),-1.0]])]});
            var Q53;
            Q53=makeQuery(id+"F0.imprint","IMPRINT",FACE,{"disambiguationData":[TD([[makeQuery(id+"F0.imprint","IMPRINT",EDGE,{"derivedFrom":sQuery(id+"F0.wireOp",EDGE,"E26.4.0")}),-1.0]])]});
            var Q54;
            Q54=makeQuery(id+"F0.imprint","IMPRINT",FACE,{"disambiguationData":[TD([[makeQuery(id+"F0.imprint","IMPRINT",EDGE,{"derivedFrom":sQuery(id+"F0.wireOp",EDGE,"E26.4.4")}),-1.0]])]});
            var Q55;
            Q55=makeQuery(id+"F0.imprint","IMPRINT",FACE,{"disambiguationData":[TD([[makeQuery(id+"F0.imprint","IMPRINT",EDGE,{"derivedFrom":sQuery(id+"F0.wireOp",EDGE,"E26.5.0")}),-1.0]])]});
            var Q56;
            Q56=makeQuery(id+"F0.imprint","IMPRINT",FACE,{"disambiguationData":[TD([[makeQuery(id+"F0.imprint","IMPRINT",EDGE,{"derivedFrom":sQuery(id+"F0.wireOp",EDGE,"E26.5.4")}),-1.0]])]});
            var Q57;
            Q57=makeQuery(id+"F0.imprint","IMPRINT",FACE,{"disambiguationData":[TD([[makeQuery(id+"F0.imprint","IMPRINT",EDGE,{"derivedFrom":sQuery(id+"F0.wireOp",EDGE,"E26.6.0")}),-1.0]])]});
            var Q58;
            Q58=makeQuery(id+"F0.imprint","IMPRINT",FACE,{"disambiguationData":[TD([[makeQuery(id+"F0.imprint","IMPRINT",EDGE,{"derivedFrom":sQuery(id+"F0.wireOp",EDGE,"E26.6.4")}),-1.0]])]});
            var Q59;
            Q59=makeQuery(id+"F0.imprint","IMPRINT",FACE,{"disambiguationData":[TD([[makeQuery(id+"F0.imprint","IMPRINT",EDGE,{"derivedFrom":sQuery(id+"F0.wireOp",EDGE,"E26.7.0")}),-1.0]])]});
            var Q60;
            Q60=makeQuery(id+"F0.imprint","IMPRINT",FACE,{"disambiguationData":[TD([[makeQuery(id+"F0.imprint","IMPRINT",EDGE,{"derivedFrom":sQuery(id+"F0.wireOp",EDGE,"E26.7.4")}),-1.0]])]});
            var Q61;
            Q61=makeQuery(id+"F0.imprint","IMPRINT",FACE,{"disambiguationData":[TD([[makeQuery(id+"F0.imprint","IMPRINT",EDGE,{"derivedFrom":sQuery(id+"F0.wireOp",EDGE,"E26.8.0")}),-1.0]])]});
            var Q62;
            Q62=makeQuery(id+"F0.imprint","IMPRINT",FACE,{"disambiguationData":[TD([[makeQuery(id+"F0.imprint","IMPRINT",EDGE,{"derivedFrom":sQuery(id+"F0.wireOp",EDGE,"E26.8.4")}),-1.0]])]});
            var Q63;
            Q63=makeQuery(id+"F0.imprint","IMPRINT",FACE,{"disambiguationData":[TD([[makeQuery(id+"F0.imprint","IMPRINT",EDGE,{"derivedFrom":sQuery(id+"F0.wireOp",EDGE,"E26.9.0")}),-1.0]])]});
            var Q64;
            Q64=makeQuery(id+"F0.imprint","IMPRINT",FACE,{"disambiguationData":[TD([[makeQuery(id+"F0.imprint","IMPRINT",EDGE,{"derivedFrom":sQuery(id+"F0.wireOp",EDGE,"E26.9.4")}),-1.0]])]});
            var Q65;
            Q65=makeQuery(id+"F0.imprint","IMPRINT",FACE,{"disambiguationData":[TD([[makeQuery(id+"F0.imprint","IMPRINT",EDGE,{"derivedFrom":sQuery(id+"F0.wireOp",EDGE,"E26.10.0")}),-1.0]])]});
            var Q66;
            Q66=makeQuery(id+"F0.imprint","IMPRINT",FACE,{"disambiguationData":[TD([[makeQuery(id+"F0.imprint","IMPRINT",EDGE,{"derivedFrom":sQuery(id+"F0.wireOp",EDGE,"E26.10.4")}),-1.0]])]});
            var Q67;
            Q67=makeQuery(id+"F0.imprint","IMPRINT",FACE,{"disambiguationData":[TD([[makeQuery(id+"F0.imprint","IMPRINT",EDGE,{"derivedFrom":sQuery(id+"F0.wireOp",EDGE,"E26.11.0")}),-1.0]])]});
            var Q68;
            Q68=makeQuery(id+"F0.imprint","IMPRINT",FACE,{"disambiguationData":[TD([[makeQuery(id+"F0.imprint","IMPRINT",EDGE,{"derivedFrom":sQuery(id+"F0.wireOp",EDGE,"E26.11.4")}),-1.0]])]});
            var Q69;
            Q69=makeQuery(id+"F0.imprint","IMPRINT",FACE,{"disambiguationData":[TD([[makeQuery(id+"F0.imprint","IMPRINT",EDGE,{"derivedFrom":sQuery(id+"F0.wireOp",EDGE,"E26.12.0")}),-1.0]])]});
            var Q70;
            Q70=makeQuery(id+"F0.imprint","IMPRINT",FACE,{"disambiguationData":[TD([[makeQuery(id+"F0.imprint","IMPRINT",EDGE,{"derivedFrom":sQuery(id+"F0.wireOp",EDGE,"E26.12.4")}),-1.0]])]});
            var Q71;
            Q71=makeQuery(id+"F0.imprint","IMPRINT",FACE,{"disambiguationData":[TD([[makeQuery(id+"F0.imprint","IMPRINT",EDGE,{"derivedFrom":sQuery(id+"F0.wireOp",EDGE,"E26.13.0")}),-1.0]])]});
            var Q72;
            Q72=makeQuery(id+"F0.imprint","IMPRINT",FACE,{"disambiguationData":[TD([[makeQuery(id+"F0.imprint","IMPRINT",EDGE,{"derivedFrom":sQuery(id+"F0.wireOp",EDGE,"E26.13.4")}),-1.0]])]});
            var Q73;
            Q73=makeQuery(id+"F0.imprint","IMPRINT",FACE,{"disambiguationData":[TD([[makeQuery(id+"F0.imprint","IMPRINT",EDGE,{"derivedFrom":sQuery(id+"F0.wireOp",EDGE,"E26.14.0")}),-1.0]])]});
            var Q74;
            Q74=makeQuery(id+"F0.imprint","IMPRINT",FACE,{"disambiguationData":[TD([[makeQuery(id+"F0.imprint","IMPRINT",EDGE,{"derivedFrom":sQuery(id+"F0.wireOp",EDGE,"E26.14.4")}),-1.0]])]});
            var Q75;
            Q75=makeQuery(id+"F0.imprint","IMPRINT",FACE,{"disambiguationData":[TD([[makeQuery(id+"F0.imprint","IMPRINT",EDGE,{"derivedFrom":sQuery(id+"F0.wireOp",EDGE,"E7.bottom")}),1.0]])]});
            extrude(context, id + "F8", {"entities" : qUnion([Q0, Q1, Q2, Q3, Q4, Q5, Q6, Q7, Q8, Q9, Q10, Q11, Q12, Q13, Q14, Q15, Q16, Q17, Q18, Q19, Q20, Q21, Q22, Q23, Q24, Q25, Q26, Q27, Q28, Q29, Q30, Q31, Q32, Q33, Q34, Q35, Q36, Q37, Q38, Q39, Q40, Q41, Q42, Q43, Q44, Q45, Q46, Q47, Q48, Q49, Q50, Q51, Q52, Q53, Q54, Q55, Q56, Q57, Q58, Q59, Q60, Q61, Q62, Q63, Q64, Q65, Q66, Q67, Q68, Q69, Q70, Q71, Q72, Q73, Q74, Q75]), "depth" : 5 * mm});
        }
        {
            var Q0;
            Q0=makeQuery(id+"F2.imprint","IMPRINT",FACE,{"disambiguationData":[TD([[makeQuery(id+"F2.imprint","IMPRINT",EDGE,{"derivedFrom":sQuery(id+"F2.wireOp",EDGE,"E38.2.1")}),-1.0]])]});
            var Q1;
            Q1=makeQuery(id+"F2.imprint","IMPRINT",FACE,{"disambiguationData":[TD([[makeQuery(id+"F2.imprint","IMPRINT",EDGE,{"derivedFrom":sQuery(id+"F2.wireOp",EDGE,"E189.0")}),1.0]])]});
            var Q2;
            Q2=makeQuery(id+"F2.imprint","IMPRINT",FACE,{"disambiguationData":[TD([[makeQuery(id+"F2.imprint","IMPRINT",EDGE,{"derivedFrom":sQuery(id+"F2.wireOp",EDGE,"E39")}),-1.0]])]});
            var Q3;
            Q3=makeQuery(id+"F2.imprint","IMPRINT",FACE,{"disambiguationData":[TD([[makeQuery(id+"F2.imprint","IMPRINT",EDGE,{"derivedFrom":sQuery(id+"F2.wireOp",EDGE,"E45.bottom")}),1.0]])]});
            extrude(context, id + "F9", {"entities" : qUnion([Q0, Q1, Q2, Q3]), "depth" : 5 * mm});
        }
    });
